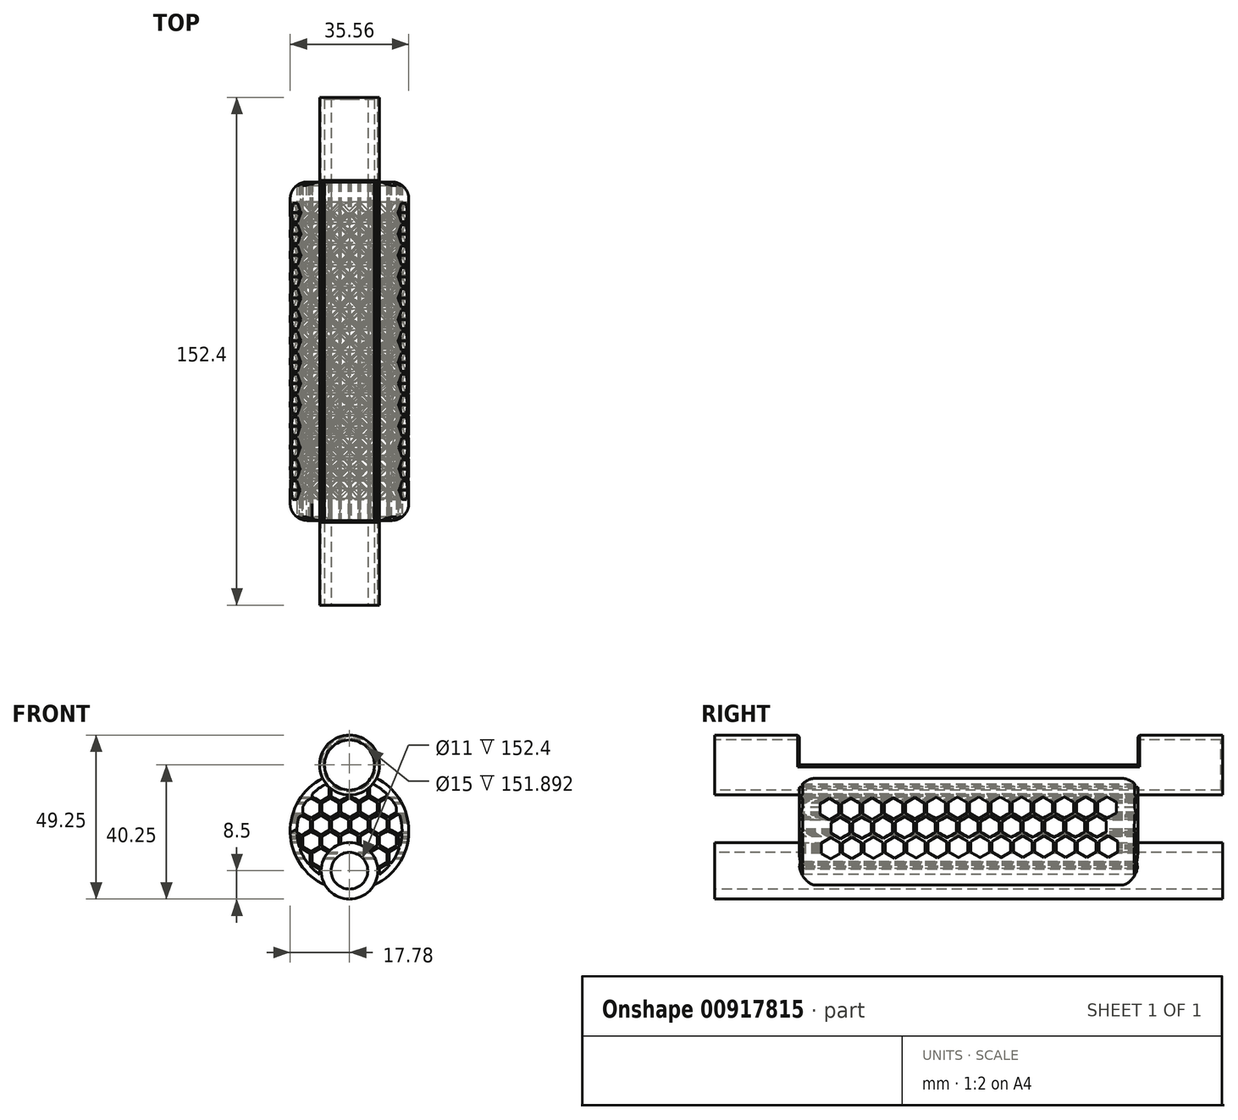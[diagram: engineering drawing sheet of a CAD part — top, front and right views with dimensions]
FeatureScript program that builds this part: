
annotation { "Feature Type Name" : "Feature", "Feature Type Description" : "" }
export const myFeature = defineFeature(function(context is Context, id is Id, definition is map)
    precondition{}
    {
        {
            var Q0;
            Q0=qCreatedBy(makeId("Front.planeOp"),FACE);
            var sketch = newSketch(context, id + "F0", { "sketchPlane" : qUnion([Q0])});
            skCircle(sketch, "E0", {"center": v(0, 0) * mm, "radius": 9 * mm});
            skCircle(sketch, "E1", {"center": v(0, -31.75) * mm, "radius": 8.5 * mm});
            skSolve(sketch);
        }
        {
            var Q0;
            Q0=qSketchRegion(id+"FUGsYxlSOq7sT89_0",true);
            var Q1;
            Q1=makeQuery(id+"F0.imprint","IMPRINT",FACE,{"disambiguationData":[TD([[makeQuery(id+"F0.imprint","IMPRINT",EDGE,{"derivedFrom":sQuery(id+"F0.wireOp",EDGE,"E0")}),1.0]])]});
            var Q2;
            Q2=makeQuery(id+"F0.imprint","IMPRINT",FACE,{"disambiguationData":[TD([[makeQuery(id+"F0.imprint","IMPRINT",EDGE,{"derivedFrom":sQuery(id+"F0.wireOp",EDGE,"E1")}),1.0]])]});
            extrude(context, id + "F1", {"entities" : qUnion([Q0, Q1, Q2]), "endBound" : BoundingType.SYMMETRIC, "depth" : 152.4 * mm, "offsetDistance" : 25.4 * mm});
        }
        {
            var Q0;
            Q0=makeQuery(id+"F1.opExtrude","CAP_FACE",FACE,{"disambiguationData":[OSD([sQuery(id+"F0.wireOp",EDGE,"E0")])],"isStart":false});
            var sketch = newSketch(context, id + "F2", { "sketchPlane" : qUnion([Q0])});
            skCircle(sketch, "E2", {"center": v(0, 0) * mm, "radius": 7.5 * mm});
            skSolve(sketch);
        }
        {
            var Q0;
            Q0=qSketchRegion(id+"F2",true);
            extrude(context, id + "F3", {"entities" : qUnion([Q0]), "operationType" : NewBodyOperationType.REMOVE, "endBound" : BoundingType.THROUGH_ALL, "oppositeDirection" : true, "depth" : 25.4 * mm, "offsetDistance" : 25.4 * mm});
        }
        {
            var Q0;
            Q0=makeQuery(id+"F0.imprint","IMPRINT",FACE,{"disambiguationData":[TD([[makeQuery(id+"F0.imprint","IMPRINT",EDGE,{"derivedFrom":sQuery(id+"F0.wireOp",EDGE,"E0")}),1.0]])]});
            var sketch = newSketch(context, id + "F4", { "sketchPlane" : qUnion([Q0])});
            skLineSegment(sketch, "E3.bottom", {"start": v(-11.18, 12.2) * mm, "end": v(12.33, 12.2) * mm});
            skLineSegment(sketch, "E3.top", {"start": v(-11.18, 0) * mm, "end": v(12.33, 0) * mm});
            skLineSegment(sketch, "E3.left", {"start": v(-11.18, 12.2) * mm, "end": v(-11.18, 0) * mm});
            skLineSegment(sketch, "E3.right", {"start": v(12.33, 12.2) * mm, "end": v(12.33, 0) * mm});
            skSolve(sketch);
        }
        {
            var Q0;
            Q0=qSketchRegion(id+"F4",true);
            extrude(context, id + "F5", {"entities" : qUnion([Q0]), "operationType" : NewBodyOperationType.REMOVE, "endBound" : BoundingType.SYMMETRIC, "oppositeDirection" : true, "depth" : 101.6 * mm, "offsetDistance" : 25.4 * mm});
        }
        {
            var Q0;
            Q0=makeQuery(id+"F5.boolean.opBoolean","INTERSECT",EDGE,{"disambiguationData":[OD(0.0)],"derivedFrom":[makeQuery(id+"F1.opExtrude","SWEPT_FACE",FACE,{"disambiguationData":[OSD([sQuery(id+"F0.wireOp",EDGE,"E0")])]}),makeQuery(id+"F5.opExtrude","SWEPT_FACE",FACE,{"disambiguationData":[OSD([sQuery(id+"F4.wireOp",EDGE,"E3.top")])]})]});
            var Q1;
            Q1=makeQuery(id+"F5.boolean.opBoolean","INTERSECT",EDGE,{"disambiguationData":[OD(1.0)],"derivedFrom":[makeQuery(id+"F1.opExtrude","SWEPT_FACE",FACE,{"disambiguationData":[OSD([sQuery(id+"F0.wireOp",EDGE,"E0")])]}),makeQuery(id+"F5.opExtrude","SWEPT_FACE",FACE,{"disambiguationData":[OSD([sQuery(id+"F4.wireOp",EDGE,"E3.top")])]})]});
            var Q2;
            Q2=makeQuery(id+"F5.boolean.opBoolean","INTERSECT",EDGE,{"disambiguationData":[OD(1.0)],"derivedFrom":[makeQuery(id+"F3.boolean.opBoolean","COPY",FACE,{"derivedFrom":makeQuery(id+"F3.opExtrude","SWEPT_FACE",FACE,{"disambiguationData":[OSD([sQuery(id+"F2.wireOp",EDGE,"E2")])]})}),makeQuery(id+"F5.opExtrude","SWEPT_FACE",FACE,{"disambiguationData":[OSD([sQuery(id+"F4.wireOp",EDGE,"E3.top")])]})]});
            var Q3;
            Q3=makeQuery(id+"F5.boolean.opBoolean","INTERSECT",EDGE,{"disambiguationData":[OD(0.0)],"derivedFrom":[makeQuery(id+"F3.boolean.opBoolean","COPY",FACE,{"derivedFrom":makeQuery(id+"F3.opExtrude","SWEPT_FACE",FACE,{"disambiguationData":[OSD([sQuery(id+"F2.wireOp",EDGE,"E2")])]})}),makeQuery(id+"F5.opExtrude","SWEPT_FACE",FACE,{"disambiguationData":[OSD([sQuery(id+"F4.wireOp",EDGE,"E3.top")])]})]});
            var Q4;
            Q4=makeQuery(id+"F5.boolean.opBoolean","INTERSECT",EDGE,{"derivedFrom":[makeQuery(id+"F1.opExtrude","SWEPT_FACE",FACE,{"disambiguationData":[OSD([sQuery(id+"F0.wireOp",EDGE,"E0")])]}),makeQuery(id+"F5.opExtrude","CAP_FACE",FACE,{"disambiguationData":[OSD([sQuery(id+"F4.wireOp",EDGE,"E3.bottom"),sQuery(id+"F4.wireOp",EDGE,"E3.top"),sQuery(id+"F4.wireOp",EDGE,"E3.left"),sQuery(id+"F4.wireOp",EDGE,"E3.right")])],"isStart":true})]});
            var Q5;
            Q5=makeQuery(id+"F5.boolean.opBoolean","INTERSECT",EDGE,{"derivedFrom":[makeQuery(id+"F1.opExtrude","SWEPT_FACE",FACE,{"disambiguationData":[OSD([sQuery(id+"F0.wireOp",EDGE,"E0")])]}),makeQuery(id+"F5.opExtrude","CAP_FACE",FACE,{"disambiguationData":[OSD([sQuery(id+"F4.wireOp",EDGE,"E3.bottom"),sQuery(id+"F4.wireOp",EDGE,"E3.top"),sQuery(id+"F4.wireOp",EDGE,"E3.left"),sQuery(id+"F4.wireOp",EDGE,"E3.right")])],"isStart":false})]});
            var Q6;
            Q6=makeQuery(id+"F5.boolean.opBoolean","INTERSECT",EDGE,{"derivedFrom":[makeQuery(id+"F3.boolean.opBoolean","COPY",FACE,{"derivedFrom":makeQuery(id+"F3.opExtrude","SWEPT_FACE",FACE,{"disambiguationData":[OSD([sQuery(id+"F2.wireOp",EDGE,"E2")])]})}),makeQuery(id+"F5.opExtrude","CAP_FACE",FACE,{"disambiguationData":[OSD([sQuery(id+"F4.wireOp",EDGE,"E3.bottom"),sQuery(id+"F4.wireOp",EDGE,"E3.top"),sQuery(id+"F4.wireOp",EDGE,"E3.left"),sQuery(id+"F4.wireOp",EDGE,"E3.right")])],"isStart":false})]});
            var Q7;
            Q7=makeQuery(id+"F5.boolean.opBoolean","INTERSECT",EDGE,{"derivedFrom":[makeQuery(id+"F3.boolean.opBoolean","COPY",FACE,{"derivedFrom":makeQuery(id+"F3.opExtrude","SWEPT_FACE",FACE,{"disambiguationData":[OSD([sQuery(id+"F2.wireOp",EDGE,"E2")])]})}),makeQuery(id+"F5.opExtrude","CAP_FACE",FACE,{"disambiguationData":[OSD([sQuery(id+"F4.wireOp",EDGE,"E3.bottom"),sQuery(id+"F4.wireOp",EDGE,"E3.top"),sQuery(id+"F4.wireOp",EDGE,"E3.left"),sQuery(id+"F4.wireOp",EDGE,"E3.right")])],"isStart":true})]});
            var Q8;
            Q8=makeQuery(id+"F3.boolean.opBoolean","INTERSECT",EDGE,{"derivedFrom":[makeQuery(id+"F1.opExtrude","CAP_FACE",FACE,{"disambiguationData":[OSD([sQuery(id+"F0.wireOp",EDGE,"E0")])],"isStart":true}),makeQuery(id+"F3.opExtrude","SWEPT_FACE",FACE,{"disambiguationData":[OSD([sQuery(id+"F2.wireOp",EDGE,"E2")])]})]});
            var Q9;
            Q9=makeQuery(id+"F3.boolean.opBoolean","COPY",EDGE,{"derivedFrom":makeQuery(id+"F3.opExtrude","CAP_EDGE",EDGE,{"disambiguationData":[OSD([sQuery(id+"F2.wireOp",EDGE,"E2")])],"isStart":true})});
            chamfer(context, id + "F6", {"entities" : qUnion([Q0, Q1, Q2, Q3, Q4, Q5, Q6, Q7, Q8, Q9]), "width" : 0.5 * mm, "tangentPropagation" : true});
        }
        {
            var Q0;
            Q0=qCreatedBy(makeId("Front.planeOp"),FACE);
            var sketch = newSketch(context, id + "F7", { "sketchPlane" : qUnion([Q0])});
            skLineSegment(sketch, "E4.0", {"start": v(2, -31.75) * mm, "end": v(2, -8.64) * mm});
            skLineSegment(sketch, "E5.0", {"start": v(-2, -31.75) * mm, "end": v(-2, -8.64) * mm});
            skPoint(sketch, "E6.start.orphan", {"position": v(0, -31.75) * mm});
            skLineSegment(sketch, "E7", {"start": v(-2, -31.75) * mm, "end": v(2, -31.75) * mm});
            skLineSegment(sketch, "E8", {"start": v(2, -8.64) * mm, "end": v(-2, -8.64) * mm});
            skSolve(sketch);
        }
        {
            var Q0;
            Q0=qSketchRegion(id+"F7",true);
            extrude(context, id + "F8", {"entities" : qUnion([Q0]), "operationType" : NewBodyOperationType.ADD, "endBound" : BoundingType.SYMMETRIC, "oppositeDirection" : true, "depth" : 101.6 * mm, "offsetDistance" : 25.4 * mm});
        }
        {
            var Q0;
            Q0=qCreatedBy(makeId("Front.planeOp"),FACE);
            var sketch = newSketch(context, id + "F9", { "sketchPlane" : qUnion([Q0])});
            skCircle(sketch, "E9", {"center": v(0, -19.81) * mm, "radius": 17.78 * mm});
            skSolve(sketch);
        }
        {
            var Q0;
            Q0=qSketchRegion(id+"F9",true);
            extrude(context, id + "F10", {"entities" : qUnion([Q0]), "operationType" : NewBodyOperationType.ADD, "endBound" : BoundingType.SYMMETRIC, "depth" : 101.6 * mm, "offsetDistance" : 25.4 * mm});
        }
        {
            var Q0;
            Q0=makeQuery(id+"F0.imprint","IMPRINT",FACE,{"disambiguationData":[TD([[makeQuery(id+"F0.imprint","IMPRINT",EDGE,{"derivedFrom":sQuery(id+"F0.wireOp",EDGE,"E0")}),1.0]])]});
            var sketch = newSketch(context, id + "F11", { "sketchPlane" : qUnion([Q0])});
            skCircle(sketch, "E10", {"center": v(0, 0) * mm, "radius": 7.5 * mm});
            skSolve(sketch);
        }
        {
            var Q0;
            Q0=qSketchRegion(id+"F11",true);
            extrude(context, id + "F12", {"entities" : qUnion([Q0]), "operationType" : NewBodyOperationType.REMOVE, "endBound" : BoundingType.SYMMETRIC, "oppositeDirection" : true, "depth" : 152.4 * mm, "offsetDistance" : 25.4 * mm});
        }
        {
            var Q0;
            Q0=makeQuery(id+"F10.boolean.opBoolean","MERGE",FACE,{"derivedFrom":[makeQuery(id+"F8.opExtrude","CAP_FACE",FACE,{"disambiguationData":[OSD([sQuery(id+"F7.wireOp",EDGE,"E4.0"),sQuery(id+"F7.wireOp",EDGE,"E5.0"),sQuery(id+"F7.wireOp",EDGE,"E7"),sQuery(id+"F7.wireOp",EDGE,"E8")])],"isStart":true}),makeQuery(id+"F10.opExtrude","CAP_FACE",FACE,{"disambiguationData":[OSD([sQuery(id+"F9.wireOp",EDGE,"E9")])],"isStart":false})]});
            var sketch = newSketch(context, id + "F13", { "sketchPlane" : qUnion([Q0])});
            skCircle(sketch, "E11.cCircle", {"center": v(-11.52, -12.94) * mm, "radius": 2.55 * mm, "construction": true});
            skLineSegment(sketch, "E11.0", {"start": v(-8.97, -11.46) * mm, "end": v(-8.97, -14.4) * mm});
            skLineSegment(sketch, "E11.1", {"start": v(-8.97, -14.4) * mm, "end": v(-11.52, -15.88) * mm});
            skLineSegment(sketch, "E11.2", {"start": v(-11.52, -15.88) * mm, "end": v(-14.07, -14.4) * mm});
            skLineSegment(sketch, "E11.3", {"start": v(-14.07, -14.4) * mm, "end": v(-14.07, -11.46) * mm});
            skLineSegment(sketch, "E11.4", {"start": v(-14.07, -11.46) * mm, "end": v(-11.52, -10) * mm});
            skLineSegment(sketch, "E11.5", {"start": v(-11.52, -10) * mm, "end": v(-8.97, -11.46) * mm});
            skPoint(sketch, "E11.0.midPoint", {"position": v(-8.97, -12.94) * mm});
            skLineSegment(sketch, "E12.1.0.0", {"start": v(-5.75, -9.92) * mm, "end": v(-3.2, -11.4) * mm});
            skLineSegment(sketch, "E12.1.0.1", {"start": v(-8.3, -11.4) * mm, "end": v(-5.75, -9.92) * mm});
            skLineSegment(sketch, "E12.1.0.2", {"start": v(-8.3, -14.34) * mm, "end": v(-8.3, -11.4) * mm});
            skLineSegment(sketch, "E12.1.0.3", {"start": v(-5.75, -15.81) * mm, "end": v(-8.3, -14.34) * mm});
            skLineSegment(sketch, "E12.1.0.4", {"start": v(-3.2, -11.4) * mm, "end": v(-3.2, -14.34) * mm});
            skLineSegment(sketch, "E12.1.0.5", {"start": v(-3.2, -14.34) * mm, "end": v(-5.75, -15.81) * mm});
            skLineSegment(sketch, "E12.2.0.0", {"start": v(0.02, -9.85) * mm, "end": v(2.57, -11.33) * mm});
            skLineSegment(sketch, "E12.2.0.1", {"start": v(-2.53, -11.33) * mm, "end": v(0.02, -9.85) * mm});
            skLineSegment(sketch, "E12.2.0.2", {"start": v(-2.53, -14.27) * mm, "end": v(-2.53, -11.33) * mm});
            skLineSegment(sketch, "E12.2.0.3", {"start": v(0.02, -15.74) * mm, "end": v(-2.53, -14.27) * mm});
            skLineSegment(sketch, "E12.2.0.4", {"start": v(2.57, -11.33) * mm, "end": v(2.57, -14.27) * mm});
            skLineSegment(sketch, "E12.2.0.5", {"start": v(2.57, -14.27) * mm, "end": v(0.02, -15.74) * mm});
            skLineSegment(sketch, "E12.3.0.0", {"start": v(5.78, -9.79) * mm, "end": v(8.33, -11.26) * mm});
            skLineSegment(sketch, "E12.3.0.1", {"start": v(3.23, -11.26) * mm, "end": v(5.78, -9.79) * mm});
            skLineSegment(sketch, "E12.3.0.2", {"start": v(3.23, -14.2) * mm, "end": v(3.23, -11.26) * mm});
            skLineSegment(sketch, "E12.3.0.3", {"start": v(5.78, -15.67) * mm, "end": v(3.23, -14.2) * mm});
            skLineSegment(sketch, "E12.3.0.4", {"start": v(8.33, -11.26) * mm, "end": v(8.33, -14.2) * mm});
            skLineSegment(sketch, "E12.3.0.5", {"start": v(8.33, -14.2) * mm, "end": v(5.78, -15.67) * mm});
            skLineSegment(sketch, "E12.4.0.0", {"start": v(11.55, -9.72) * mm, "end": v(14.1, -11.19) * mm});
            skLineSegment(sketch, "E12.4.0.1", {"start": v(9, -11.19) * mm, "end": v(11.55, -9.72) * mm});
            skLineSegment(sketch, "E12.4.0.2", {"start": v(9, -14.13) * mm, "end": v(9, -11.19) * mm});
            skLineSegment(sketch, "E12.4.0.3", {"start": v(11.55, -15.6) * mm, "end": v(9, -14.13) * mm});
            skLineSegment(sketch, "E12.4.0.4", {"start": v(14.1, -11.19) * mm, "end": v(14.1, -14.13) * mm});
            skLineSegment(sketch, "E12.4.0.5", {"start": v(14.1, -14.13) * mm, "end": v(11.55, -15.6) * mm});
            skLineSegment(sketch, "E12.direction1", {"start": v(-11.52, -10) * mm, "end": v(-5.75, -9.92) * mm, "construction": true});
            skSolve(sketch);
        }
        {
            var Q0;
            Q0=qSketchRegion(id+"F13",true);
            extrude(context, id + "F14", {"entities" : qUnion([Q0]), "operationType" : NewBodyOperationType.REMOVE, "oppositeDirection" : true, "depth" : 177.8 * mm, "offsetDistance" : 25.4 * mm});
        }
        {
            var Q0;
            Q0=makeQuery(id+"F10.boolean.opBoolean","MERGE",FACE,{"derivedFrom":[makeQuery(id+"F8.opExtrude","CAP_FACE",FACE,{"disambiguationData":[OSD([sQuery(id+"F7.wireOp",EDGE,"E4.0"),sQuery(id+"F7.wireOp",EDGE,"E5.0"),sQuery(id+"F7.wireOp",EDGE,"E7"),sQuery(id+"F7.wireOp",EDGE,"E8")])],"isStart":true}),makeQuery(id+"F10.opExtrude","CAP_FACE",FACE,{"disambiguationData":[OSD([sQuery(id+"F9.wireOp",EDGE,"E9")])],"isStart":false})]});
            var sketch = newSketch(context, id + "F15", { "sketchPlane" : qUnion([Q0])});
            skCircle(sketch, "E13.cCircle", {"center": v(-14.33, -18.09) * mm, "radius": 2.55 * mm, "construction": true});
            skLineSegment(sketch, "E13.0", {"start": v(-11.78, -16.61) * mm, "end": v(-11.78, -19.56) * mm});
            skLineSegment(sketch, "E13.1", {"start": v(-11.78, -19.56) * mm, "end": v(-14.33, -21.03) * mm});
            skLineSegment(sketch, "E13.2", {"start": v(-14.33, -21.03) * mm, "end": v(-16.88, -19.56) * mm});
            skLineSegment(sketch, "E13.3", {"start": v(-16.88, -19.56) * mm, "end": v(-16.88, -16.61) * mm});
            skLineSegment(sketch, "E13.4", {"start": v(-16.88, -16.61) * mm, "end": v(-14.33, -15.14) * mm});
            skLineSegment(sketch, "E13.5", {"start": v(-14.33, -15.14) * mm, "end": v(-11.78, -16.61) * mm});
            skPoint(sketch, "E13.0.midPoint", {"position": v(-11.78, -18.09) * mm});
            skLineSegment(sketch, "E14.1.0.0", {"start": v(-8.56, -15.07) * mm, "end": v(-6.01, -16.55) * mm});
            skLineSegment(sketch, "E14.1.0.1", {"start": v(-11.11, -16.55) * mm, "end": v(-8.56, -15.07) * mm});
            skLineSegment(sketch, "E14.1.0.2", {"start": v(-11.11, -19.5) * mm, "end": v(-11.11, -16.55) * mm});
            skLineSegment(sketch, "E14.1.0.3", {"start": v(-8.56, -20.96) * mm, "end": v(-11.11, -19.5) * mm});
            skLineSegment(sketch, "E14.1.0.4", {"start": v(-6.01, -16.55) * mm, "end": v(-6.01, -19.5) * mm});
            skLineSegment(sketch, "E14.1.0.5", {"start": v(-6.01, -19.5) * mm, "end": v(-8.56, -20.96) * mm});
            skLineSegment(sketch, "E14.2.0.0", {"start": v(-2.8, -15) * mm, "end": v(-0.25, -16.48) * mm});
            skLineSegment(sketch, "E14.2.0.1", {"start": v(-5.35, -16.48) * mm, "end": v(-2.8, -15) * mm});
            skLineSegment(sketch, "E14.2.0.2", {"start": v(-5.35, -19.42) * mm, "end": v(-5.35, -16.48) * mm});
            skLineSegment(sketch, "E14.2.0.3", {"start": v(-2.8, -20.9) * mm, "end": v(-5.35, -19.42) * mm});
            skLineSegment(sketch, "E14.2.0.4", {"start": v(-0.25, -16.48) * mm, "end": v(-0.25, -19.42) * mm});
            skLineSegment(sketch, "E14.2.0.5", {"start": v(-0.25, -19.42) * mm, "end": v(-2.8, -20.9) * mm});
            skLineSegment(sketch, "E14.3.0.0", {"start": v(2.97, -14.94) * mm, "end": v(5.52, -16.4) * mm});
            skLineSegment(sketch, "E14.3.0.1", {"start": v(0.42, -16.4) * mm, "end": v(2.97, -14.94) * mm});
            skLineSegment(sketch, "E14.3.0.2", {"start": v(0.42, -19.35) * mm, "end": v(0.42, -16.4) * mm});
            skLineSegment(sketch, "E14.3.0.3", {"start": v(2.97, -20.83) * mm, "end": v(0.42, -19.35) * mm});
            skLineSegment(sketch, "E14.3.0.4", {"start": v(5.52, -16.4) * mm, "end": v(5.52, -19.35) * mm});
            skLineSegment(sketch, "E14.3.0.5", {"start": v(5.52, -19.35) * mm, "end": v(2.97, -20.83) * mm});
            skLineSegment(sketch, "E14.4.0.0", {"start": v(8.73, -14.87) * mm, "end": v(11.28, -16.34) * mm});
            skLineSegment(sketch, "E14.4.0.1", {"start": v(6.18, -16.34) * mm, "end": v(8.73, -14.87) * mm});
            skLineSegment(sketch, "E14.4.0.2", {"start": v(6.18, -19.28) * mm, "end": v(6.18, -16.34) * mm});
            skLineSegment(sketch, "E14.4.0.3", {"start": v(8.73, -20.76) * mm, "end": v(6.18, -19.28) * mm});
            skLineSegment(sketch, "E14.4.0.4", {"start": v(11.28, -16.34) * mm, "end": v(11.28, -19.28) * mm});
            skLineSegment(sketch, "E14.4.0.5", {"start": v(11.28, -19.28) * mm, "end": v(8.73, -20.76) * mm});
            skLineSegment(sketch, "E14.direction1", {"start": v(-14.33, -15.14) * mm, "end": v(-8.56, -15.07) * mm, "construction": true});
            skLineSegment(sketch, "E15.0.5.0", {"start": v(14.5, -14.8) * mm, "end": v(17.05, -16.27) * mm});
            skLineSegment(sketch, "E15.3.5.0", {"start": v(11.95, -16.27) * mm, "end": v(14.5, -14.8) * mm});
            skLineSegment(sketch, "E15.6.5.0", {"start": v(11.95, -19.22) * mm, "end": v(11.95, -16.27) * mm});
            skLineSegment(sketch, "E15.9.5.0", {"start": v(14.5, -20.69) * mm, "end": v(11.95, -19.22) * mm});
            skLineSegment(sketch, "E15.12.5.0", {"start": v(17.05, -16.27) * mm, "end": v(17.05, -19.22) * mm});
            skLineSegment(sketch, "E15.15.5.0", {"start": v(17.05, -19.22) * mm, "end": v(14.5, -20.69) * mm});
            skSolve(sketch);
        }
        {
            var Q0;
            Q0=qSketchRegion(id+"F15",true);
            extrude(context, id + "F16", {"entities" : qUnion([Q0]), "operationType" : NewBodyOperationType.REMOVE, "oppositeDirection" : true, "depth" : 177.8 * mm, "offsetDistance" : 25.4 * mm});
        }
        {
            var Q0;
            Q0=makeQuery(id+"F10.boolean.opBoolean","MERGE",FACE,{"derivedFrom":[makeQuery(id+"F8.opExtrude","CAP_FACE",FACE,{"disambiguationData":[OSD([sQuery(id+"F7.wireOp",EDGE,"E4.0"),sQuery(id+"F7.wireOp",EDGE,"E5.0"),sQuery(id+"F7.wireOp",EDGE,"E7"),sQuery(id+"F7.wireOp",EDGE,"E8")])],"isStart":true}),makeQuery(id+"F10.opExtrude","CAP_FACE",FACE,{"disambiguationData":[OSD([sQuery(id+"F9.wireOp",EDGE,"E9")])],"isStart":false})]});
            var sketch = newSketch(context, id + "F17", { "sketchPlane" : qUnion([Q0])});
            skCircle(sketch, "E16.cCircle", {"center": v(-17.3, -23) * mm, "radius": 2.55 * mm, "construction": true});
            skLineSegment(sketch, "E16.0", {"start": v(-14.75, -21.52) * mm, "end": v(-14.75, -24.47) * mm});
            skLineSegment(sketch, "E16.1", {"start": v(-14.75, -24.47) * mm, "end": v(-17.3, -25.94) * mm});
            skLineSegment(sketch, "E16.2", {"start": v(-17.3, -25.94) * mm, "end": v(-19.84, -24.47) * mm});
            skLineSegment(sketch, "E16.3", {"start": v(-19.84, -24.47) * mm, "end": v(-19.84, -21.52) * mm});
            skLineSegment(sketch, "E16.4", {"start": v(-19.84, -21.52) * mm, "end": v(-17.3, -20.05) * mm});
            skLineSegment(sketch, "E16.5", {"start": v(-17.3, -20.05) * mm, "end": v(-14.75, -21.52) * mm});
            skPoint(sketch, "E16.0.midPoint", {"position": v(-14.75, -23) * mm});
            skLineSegment(sketch, "E17.1.0.0", {"start": v(-11.53, -19.98) * mm, "end": v(-8.98, -21.46) * mm});
            skLineSegment(sketch, "E17.1.0.1", {"start": v(-14.08, -21.46) * mm, "end": v(-11.53, -19.98) * mm});
            skLineSegment(sketch, "E17.1.0.2", {"start": v(-14.08, -24.4) * mm, "end": v(-14.08, -21.46) * mm});
            skLineSegment(sketch, "E17.1.0.3", {"start": v(-11.53, -25.87) * mm, "end": v(-14.08, -24.4) * mm});
            skLineSegment(sketch, "E17.1.0.4", {"start": v(-8.98, -21.46) * mm, "end": v(-8.98, -24.4) * mm});
            skLineSegment(sketch, "E17.1.0.5", {"start": v(-8.98, -24.4) * mm, "end": v(-11.53, -25.87) * mm});
            skLineSegment(sketch, "E17.direction1", {"start": v(-17.3, -20.05) * mm, "end": v(-11.53, -19.98) * mm, "construction": true});
            skLineSegment(sketch, "E18.0.2.0", {"start": v(-5.76, -19.91) * mm, "end": v(-3.21, -21.39) * mm});
            skLineSegment(sketch, "E18.3.2.0", {"start": v(-8.31, -21.39) * mm, "end": v(-5.76, -19.91) * mm});
            skLineSegment(sketch, "E18.6.2.0", {"start": v(-8.31, -24.33) * mm, "end": v(-8.31, -21.39) * mm});
            skLineSegment(sketch, "E18.9.2.0", {"start": v(-5.76, -25.8) * mm, "end": v(-8.31, -24.33) * mm});
            skLineSegment(sketch, "E18.12.2.0", {"start": v(-3.21, -21.39) * mm, "end": v(-3.21, -24.33) * mm});
            skLineSegment(sketch, "E18.15.2.0", {"start": v(-3.21, -24.33) * mm, "end": v(-5.76, -25.8) * mm});
            skLineSegment(sketch, "E18.0.3.0", {"start": v(0, -19.85) * mm, "end": v(2.55, -21.32) * mm});
            skLineSegment(sketch, "E18.3.3.0", {"start": v(-2.55, -21.32) * mm, "end": v(0, -19.85) * mm});
            skLineSegment(sketch, "E18.6.3.0", {"start": v(-2.55, -24.26) * mm, "end": v(-2.55, -21.32) * mm});
            skLineSegment(sketch, "E18.9.3.0", {"start": v(0, -25.74) * mm, "end": v(-2.55, -24.26) * mm});
            skLineSegment(sketch, "E18.12.3.0", {"start": v(2.55, -21.32) * mm, "end": v(2.55, -24.26) * mm});
            skLineSegment(sketch, "E18.15.3.0", {"start": v(2.55, -24.26) * mm, "end": v(0, -25.74) * mm});
            skLineSegment(sketch, "E18.0.4.0", {"start": v(5.77, -19.78) * mm, "end": v(8.32, -21.25) * mm});
            skLineSegment(sketch, "E18.3.4.0", {"start": v(3.22, -21.25) * mm, "end": v(5.77, -19.78) * mm});
            skLineSegment(sketch, "E18.6.4.0", {"start": v(3.22, -24.2) * mm, "end": v(3.22, -21.25) * mm});
            skLineSegment(sketch, "E18.9.4.0", {"start": v(5.77, -25.67) * mm, "end": v(3.22, -24.2) * mm});
            skLineSegment(sketch, "E18.12.4.0", {"start": v(8.32, -21.25) * mm, "end": v(8.32, -24.2) * mm});
            skLineSegment(sketch, "E18.15.4.0", {"start": v(8.32, -24.2) * mm, "end": v(5.77, -25.67) * mm});
            skLineSegment(sketch, "E19.0.5.0", {"start": v(11.53, -19.7) * mm, "end": v(14.08, -21.18) * mm});
            skLineSegment(sketch, "E19.3.5.0", {"start": v(8.98, -21.18) * mm, "end": v(11.53, -19.7) * mm});
            skLineSegment(sketch, "E19.6.5.0", {"start": v(8.98, -24.13) * mm, "end": v(8.98, -21.18) * mm});
            skLineSegment(sketch, "E19.9.5.0", {"start": v(11.53, -25.6) * mm, "end": v(8.98, -24.13) * mm});
            skLineSegment(sketch, "E19.12.5.0", {"start": v(14.08, -21.18) * mm, "end": v(14.08, -24.13) * mm});
            skLineSegment(sketch, "E19.15.5.0", {"start": v(14.08, -24.13) * mm, "end": v(11.53, -25.6) * mm});
            skLineSegment(sketch, "E20.0.6.0", {"start": v(17.3, -19.64) * mm, "end": v(19.85, -21.11) * mm});
            skLineSegment(sketch, "E20.3.6.0", {"start": v(14.75, -21.11) * mm, "end": v(17.3, -19.64) * mm});
            skLineSegment(sketch, "E20.6.6.0", {"start": v(14.75, -24.06) * mm, "end": v(14.75, -21.11) * mm});
            skLineSegment(sketch, "E20.9.6.0", {"start": v(17.3, -25.53) * mm, "end": v(14.75, -24.06) * mm});
            skLineSegment(sketch, "E20.12.6.0", {"start": v(19.85, -21.11) * mm, "end": v(19.85, -24.06) * mm});
            skLineSegment(sketch, "E20.15.6.0", {"start": v(19.85, -24.06) * mm, "end": v(17.3, -25.53) * mm});
            skSolve(sketch);
        }
        {
            var Q0;
            {var subQ6=sQuery(id+"F17.wireOp",EDGE,"E16.0");Q0=makeQuery(id+"F17.imprint","IMPRINT",FACE,{"disambiguationData":[TD([[makeQuery(id+"F17.imprint","IMPRINT",EDGE,{"derivedFrom":subQ6}),-1.0]])]});}
            var Q1;
            Q1=makeQuery(id+"F17.imprint","IMPRINT",FACE,{"disambiguationData":[TD([[makeQuery(id+"F17.imprint","IMPRINT",EDGE,{"derivedFrom":sQuery(id+"F17.wireOp",EDGE,"E17.1.0.0")}),-1.0]])]});
            var Q2;
            {var subQ4=sQuery(id+"F17.wireOp",EDGE,"E18.0.2.0");Q2=makeQuery(id+"F17.imprint","IMPRINT",FACE,{"disambiguationData":[TD([[makeQuery(id+"F17.imprint","IMPRINT",EDGE,{"derivedFrom":subQ4}),-1.0]])]});}
            var Q3;
            {var subQ5=sQuery(id+"F17.wireOp",EDGE,"E18.0.3.0");Q3=makeQuery(id+"F17.imprint","IMPRINT",FACE,{"disambiguationData":[TD([[makeQuery(id+"F17.imprint","IMPRINT",EDGE,{"derivedFrom":subQ5}),-1.0]])]});}
            var Q4;
            Q4=makeQuery(id+"F17.imprint","IMPRINT",FACE,{"disambiguationData":[TD([[makeQuery(id+"F17.imprint","IMPRINT",EDGE,{"derivedFrom":sQuery(id+"F17.wireOp",EDGE,"E18.0.4.0")}),-1.0]])]});
            var Q5;
            Q5=makeQuery(id+"F17.imprint","IMPRINT",FACE,{"disambiguationData":[TD([[makeQuery(id+"F17.imprint","IMPRINT",EDGE,{"derivedFrom":sQuery(id+"F17.wireOp",EDGE,"E19.0.5.0")}),-1.0]])]});
            var Q6;
            {var subQ1=sQuery(id+"F17.wireOp",EDGE,"E20.3.6.0");Q6=makeQuery(id+"F17.imprint","IMPRINT",FACE,{"disambiguationData":[TD([[makeQuery(id+"F17.imprint","IMPRINT",EDGE,{"derivedFrom":subQ1}),-1.0]])]});}
            extrude(context, id + "F18", {"entities" : qUnion([Q0, Q1, Q2, Q3, Q4, Q5, Q6]), "operationType" : NewBodyOperationType.REMOVE, "oppositeDirection" : true, "depth" : 101.6 * mm, "offsetDistance" : 25.4 * mm});
        }
        {
            var Q0;
            Q0=makeQuery(id+"F10.boolean.opBoolean","MERGE",FACE,{"derivedFrom":[makeQuery(id+"F8.opExtrude","CAP_FACE",FACE,{"disambiguationData":[OSD([sQuery(id+"F7.wireOp",EDGE,"E4.0"),sQuery(id+"F7.wireOp",EDGE,"E5.0"),sQuery(id+"F7.wireOp",EDGE,"E7"),sQuery(id+"F7.wireOp",EDGE,"E8")])],"isStart":true}),makeQuery(id+"F10.opExtrude","CAP_FACE",FACE,{"disambiguationData":[OSD([sQuery(id+"F9.wireOp",EDGE,"E9")])],"isStart":false})]});
            var sketch = newSketch(context, id + "F19", { "sketchPlane" : qUnion([Q0])});
            skCircle(sketch, "E21.cCircle", {"center": v(-14.4, -27.92) * mm, "radius": 2.55 * mm, "construction": true});
            skLineSegment(sketch, "E21.0", {"start": v(-11.84, -26.45) * mm, "end": v(-11.84, -29.4) * mm});
            skLineSegment(sketch, "E21.1", {"start": v(-11.84, -29.4) * mm, "end": v(-14.4, -30.86) * mm});
            skLineSegment(sketch, "E21.2", {"start": v(-14.4, -30.86) * mm, "end": v(-16.94, -29.4) * mm});
            skLineSegment(sketch, "E21.3", {"start": v(-16.94, -29.4) * mm, "end": v(-16.94, -26.45) * mm});
            skLineSegment(sketch, "E21.4", {"start": v(-16.94, -26.45) * mm, "end": v(-14.4, -24.98) * mm});
            skLineSegment(sketch, "E21.5", {"start": v(-14.4, -24.98) * mm, "end": v(-11.84, -26.45) * mm});
            skPoint(sketch, "E21.0.midPoint", {"position": v(-11.84, -27.92) * mm});
            skLineSegment(sketch, "E22.1.0.0", {"start": v(-8.63, -24.9) * mm, "end": v(-6.08, -26.38) * mm});
            skLineSegment(sketch, "E22.1.0.1", {"start": v(-11.18, -26.38) * mm, "end": v(-8.63, -24.9) * mm});
            skLineSegment(sketch, "E22.1.0.2", {"start": v(-11.18, -29.32) * mm, "end": v(-11.18, -26.38) * mm});
            skLineSegment(sketch, "E22.1.0.3", {"start": v(-8.63, -30.8) * mm, "end": v(-11.18, -29.32) * mm});
            skLineSegment(sketch, "E22.1.0.4", {"start": v(-6.08, -26.38) * mm, "end": v(-6.08, -29.32) * mm});
            skLineSegment(sketch, "E22.1.0.5", {"start": v(-6.08, -29.32) * mm, "end": v(-8.63, -30.8) * mm});
            skLineSegment(sketch, "E22.2.0.0", {"start": v(-2.86, -24.84) * mm, "end": v(-0.31, -26.31) * mm});
            skLineSegment(sketch, "E22.2.0.1", {"start": v(-5.41, -26.31) * mm, "end": v(-2.86, -24.84) * mm});
            skLineSegment(sketch, "E22.2.0.2", {"start": v(-5.41, -29.25) * mm, "end": v(-5.41, -26.31) * mm});
            skLineSegment(sketch, "E22.2.0.3", {"start": v(-2.86, -30.73) * mm, "end": v(-5.41, -29.25) * mm});
            skLineSegment(sketch, "E22.2.0.4", {"start": v(-0.31, -26.31) * mm, "end": v(-0.31, -29.25) * mm});
            skLineSegment(sketch, "E22.2.0.5", {"start": v(-0.31, -29.25) * mm, "end": v(-2.86, -30.73) * mm});
            skLineSegment(sketch, "E22.3.0.0", {"start": v(2.9, -24.77) * mm, "end": v(5.45, -26.24) * mm});
            skLineSegment(sketch, "E22.3.0.1", {"start": v(0.35, -26.24) * mm, "end": v(2.9, -24.77) * mm});
            skLineSegment(sketch, "E22.3.0.2", {"start": v(0.35, -29.19) * mm, "end": v(0.35, -26.24) * mm});
            skLineSegment(sketch, "E22.3.0.3", {"start": v(2.9, -30.66) * mm, "end": v(0.35, -29.19) * mm});
            skLineSegment(sketch, "E22.3.0.4", {"start": v(5.45, -26.24) * mm, "end": v(5.45, -29.19) * mm});
            skLineSegment(sketch, "E22.3.0.5", {"start": v(5.45, -29.19) * mm, "end": v(2.9, -30.66) * mm});
            skLineSegment(sketch, "E22.4.0.0", {"start": v(8.67, -24.7) * mm, "end": v(11.22, -26.17) * mm});
            skLineSegment(sketch, "E22.4.0.1", {"start": v(6.12, -26.17) * mm, "end": v(8.67, -24.7) * mm});
            skLineSegment(sketch, "E22.4.0.2", {"start": v(6.12, -29.12) * mm, "end": v(6.12, -26.17) * mm});
            skLineSegment(sketch, "E22.4.0.3", {"start": v(8.67, -30.6) * mm, "end": v(6.12, -29.12) * mm});
            skLineSegment(sketch, "E22.4.0.4", {"start": v(11.22, -26.17) * mm, "end": v(11.22, -29.12) * mm});
            skLineSegment(sketch, "E22.4.0.5", {"start": v(11.22, -29.12) * mm, "end": v(8.67, -30.6) * mm});
            skLineSegment(sketch, "E22.direction1", {"start": v(-14.4, -24.98) * mm, "end": v(-8.63, -24.9) * mm, "construction": true});
            skLineSegment(sketch, "E23.0.5.0", {"start": v(14.44, -24.63) * mm, "end": v(16.99, -26.1) * mm});
            skLineSegment(sketch, "E23.3.5.0", {"start": v(11.89, -26.1) * mm, "end": v(14.44, -24.63) * mm});
            skLineSegment(sketch, "E23.6.5.0", {"start": v(11.89, -29.05) * mm, "end": v(11.89, -26.1) * mm});
            skLineSegment(sketch, "E23.9.5.0", {"start": v(14.44, -30.52) * mm, "end": v(11.89, -29.05) * mm});
            skLineSegment(sketch, "E23.12.5.0", {"start": v(16.99, -26.1) * mm, "end": v(16.99, -29.05) * mm});
            skLineSegment(sketch, "E23.15.5.0", {"start": v(16.99, -29.05) * mm, "end": v(14.44, -30.52) * mm});
            skSolve(sketch);
        }
        {
            var Q0;
            Q0=makeQuery(id+"F19.imprint","IMPRINT",FACE,{"disambiguationData":[TD([[makeQuery(id+"F19.imprint","IMPRINT",EDGE,{"derivedFrom":sQuery(id+"F19.wireOp",EDGE,"E21.0")}),1.0]])]});
            var sketch = newSketch(context, id + "F20", { "sketchPlane" : qUnion([Q0])});
            skCircle(sketch, "E24.cCircle", {"center": v(-8.71, -8) * mm, "radius": 2.55 * mm, "construction": true});
            skLineSegment(sketch, "E24.0", {"start": v(-6.16, -6.53) * mm, "end": v(-6.16, -9.47) * mm});
            skLineSegment(sketch, "E24.1", {"start": v(-6.16, -9.47) * mm, "end": v(-8.71, -10.94) * mm});
            skLineSegment(sketch, "E24.2", {"start": v(-8.71, -10.94) * mm, "end": v(-11.26, -9.47) * mm});
            skLineSegment(sketch, "E24.3", {"start": v(-11.26, -9.47) * mm, "end": v(-11.26, -6.53) * mm});
            skLineSegment(sketch, "E24.4", {"start": v(-11.26, -6.53) * mm, "end": v(-8.71, -5.06) * mm});
            skLineSegment(sketch, "E24.5", {"start": v(-8.71, -5.06) * mm, "end": v(-6.16, -6.53) * mm});
            skPoint(sketch, "E24.0.midPoint", {"position": v(-6.16, -8) * mm});
            skLineSegment(sketch, "E25.1.0.0", {"start": v(-2.95, -4.99) * mm, "end": v(-0.4, -6.46) * mm});
            skLineSegment(sketch, "E25.1.0.1", {"start": v(-5.5, -6.46) * mm, "end": v(-2.95, -4.99) * mm});
            skLineSegment(sketch, "E25.1.0.2", {"start": v(-5.5, -9.4) * mm, "end": v(-5.5, -6.46) * mm});
            skLineSegment(sketch, "E25.1.0.3", {"start": v(-2.95, -10.88) * mm, "end": v(-5.5, -9.4) * mm});
            skLineSegment(sketch, "E25.1.0.4", {"start": v(-0.4, -6.46) * mm, "end": v(-0.4, -9.4) * mm});
            skLineSegment(sketch, "E25.1.0.5", {"start": v(-0.4, -9.4) * mm, "end": v(-2.95, -10.88) * mm});
            skLineSegment(sketch, "E25.2.0.0", {"start": v(2.82, -4.92) * mm, "end": v(5.37, -6.4) * mm});
            skLineSegment(sketch, "E25.2.0.1", {"start": v(0.27, -6.4) * mm, "end": v(2.82, -4.92) * mm});
            skLineSegment(sketch, "E25.2.0.2", {"start": v(0.27, -9.34) * mm, "end": v(0.27, -6.4) * mm});
            skLineSegment(sketch, "E25.2.0.3", {"start": v(2.82, -10.8) * mm, "end": v(0.27, -9.34) * mm});
            skLineSegment(sketch, "E25.2.0.4", {"start": v(5.37, -6.4) * mm, "end": v(5.37, -9.34) * mm});
            skLineSegment(sketch, "E25.2.0.5", {"start": v(5.37, -9.34) * mm, "end": v(2.82, -10.8) * mm});
            skLineSegment(sketch, "E25.3.0.0", {"start": v(8.59, -4.85) * mm, "end": v(11.14, -6.32) * mm});
            skLineSegment(sketch, "E25.3.0.1", {"start": v(6.04, -6.32) * mm, "end": v(8.59, -4.85) * mm});
            skLineSegment(sketch, "E25.3.0.2", {"start": v(6.04, -9.27) * mm, "end": v(6.04, -6.32) * mm});
            skLineSegment(sketch, "E25.3.0.3", {"start": v(8.59, -10.74) * mm, "end": v(6.04, -9.27) * mm});
            skLineSegment(sketch, "E25.3.0.4", {"start": v(11.14, -6.32) * mm, "end": v(11.14, -9.27) * mm});
            skLineSegment(sketch, "E25.3.0.5", {"start": v(11.14, -9.27) * mm, "end": v(8.59, -10.74) * mm});
            skLineSegment(sketch, "E25.direction1", {"start": v(-8.71, -5.06) * mm, "end": v(-2.95, -4.99) * mm, "construction": true});
            skSolve(sketch);
        }
        {
            var Q0;
            {var subQ30=sQuery(id+"F20.wireOp",EDGE,"E24.1");Q0=makeQuery(id+"F20.imprint","IMPRINT",FACE,{"disambiguationData":[TD([[makeQuery(id+"F20.imprint","IMPRINT",EDGE,{"derivedFrom":subQ30}),1.0]])]});}
            var sketch = newSketch(context, id + "F21", { "sketchPlane" : qUnion([Q0])});
            skCircle(sketch, "E26.cCircle", {"center": v(-11.51, -32.84) * mm, "radius": 2.55 * mm, "construction": true});
            skLineSegment(sketch, "E26.0", {"start": v(-8.96, -31.36) * mm, "end": v(-8.96, -34.3) * mm});
            skLineSegment(sketch, "E26.1", {"start": v(-8.96, -34.3) * mm, "end": v(-11.51, -35.78) * mm});
            skLineSegment(sketch, "E26.2", {"start": v(-11.51, -35.78) * mm, "end": v(-14.06, -34.3) * mm});
            skLineSegment(sketch, "E26.3", {"start": v(-14.06, -34.3) * mm, "end": v(-14.06, -31.36) * mm});
            skLineSegment(sketch, "E26.4", {"start": v(-14.06, -31.36) * mm, "end": v(-11.51, -29.9) * mm});
            skLineSegment(sketch, "E26.5", {"start": v(-11.51, -29.9) * mm, "end": v(-8.96, -31.36) * mm});
            skPoint(sketch, "E26.0.midPoint", {"position": v(-8.96, -32.84) * mm});
            skLineSegment(sketch, "E27.1.0.0", {"start": v(-5.75, -29.82) * mm, "end": v(-3.2, -31.3) * mm});
            skLineSegment(sketch, "E27.1.0.1", {"start": v(-8.3, -31.3) * mm, "end": v(-5.75, -29.82) * mm});
            skLineSegment(sketch, "E27.1.0.2", {"start": v(-8.3, -34.24) * mm, "end": v(-8.3, -31.3) * mm});
            skLineSegment(sketch, "E27.1.0.3", {"start": v(-5.75, -35.71) * mm, "end": v(-8.3, -34.24) * mm});
            skLineSegment(sketch, "E27.1.0.4", {"start": v(-3.2, -31.3) * mm, "end": v(-3.2, -34.24) * mm});
            skLineSegment(sketch, "E27.1.0.5", {"start": v(-3.2, -34.24) * mm, "end": v(-5.75, -35.71) * mm});
            skLineSegment(sketch, "E27.2.0.0", {"start": v(0.02, -29.75) * mm, "end": v(2.57, -31.23) * mm});
            skLineSegment(sketch, "E27.2.0.1", {"start": v(-2.53, -31.23) * mm, "end": v(0.02, -29.75) * mm});
            skLineSegment(sketch, "E27.2.0.2", {"start": v(-2.53, -34.17) * mm, "end": v(-2.53, -31.23) * mm});
            skLineSegment(sketch, "E27.2.0.3", {"start": v(0.02, -35.64) * mm, "end": v(-2.53, -34.17) * mm});
            skLineSegment(sketch, "E27.2.0.4", {"start": v(2.57, -31.23) * mm, "end": v(2.57, -34.17) * mm});
            skLineSegment(sketch, "E27.2.0.5", {"start": v(2.57, -34.17) * mm, "end": v(0.02, -35.64) * mm});
            skLineSegment(sketch, "E27.3.0.0", {"start": v(5.79, -29.69) * mm, "end": v(8.34, -31.16) * mm});
            skLineSegment(sketch, "E27.3.0.1", {"start": v(3.24, -31.16) * mm, "end": v(5.79, -29.69) * mm});
            skLineSegment(sketch, "E27.3.0.2", {"start": v(3.24, -34.1) * mm, "end": v(3.24, -31.16) * mm});
            skLineSegment(sketch, "E27.3.0.3", {"start": v(5.79, -35.57) * mm, "end": v(3.24, -34.1) * mm});
            skLineSegment(sketch, "E27.3.0.4", {"start": v(8.34, -31.16) * mm, "end": v(8.34, -34.1) * mm});
            skLineSegment(sketch, "E27.3.0.5", {"start": v(8.34, -34.1) * mm, "end": v(5.79, -35.57) * mm});
            skLineSegment(sketch, "E27.direction1", {"start": v(-11.51, -29.9) * mm, "end": v(-5.75, -29.82) * mm, "construction": true});
            skLineSegment(sketch, "E28.0.4.0", {"start": v(11.55, -29.62) * mm, "end": v(14.1, -31.09) * mm});
            skLineSegment(sketch, "E28.3.4.0", {"start": v(9, -31.09) * mm, "end": v(11.55, -29.62) * mm});
            skLineSegment(sketch, "E28.6.4.0", {"start": v(9, -34.03) * mm, "end": v(9, -31.09) * mm});
            skLineSegment(sketch, "E28.9.4.0", {"start": v(11.55, -35.5) * mm, "end": v(9, -34.03) * mm});
            skLineSegment(sketch, "E28.12.4.0", {"start": v(14.1, -31.09) * mm, "end": v(14.1, -34.03) * mm});
            skLineSegment(sketch, "E28.15.4.0", {"start": v(14.1, -34.03) * mm, "end": v(11.55, -35.5) * mm});
            skSolve(sketch);
        }
        {
            var Q0;
            {var subQ4=sQuery(id+"F20.wireOp",EDGE,"E25.1.0.3");Q0=makeQuery(id+"F20.imprint","IMPRINT",FACE,{"disambiguationData":[TD([[makeQuery(id+"F20.imprint","IMPRINT",EDGE,{"derivedFrom":subQ4}),-1.0]])]});}
            var Q1;
            {var subQ4=sQuery(id+"F20.wireOp",EDGE,"E25.2.0.3");Q1=makeQuery(id+"F20.imprint","IMPRINT",FACE,{"disambiguationData":[TD([[makeQuery(id+"F20.imprint","IMPRINT",EDGE,{"derivedFrom":subQ4}),-1.0]])]});}
            var Q2;
            {var subQ5=sQuery(id+"F20.wireOp",EDGE,"E25.3.0.0");Q2=makeQuery(id+"F20.imprint","IMPRINT",FACE,{"disambiguationData":[TD([[makeQuery(id+"F20.imprint","IMPRINT",EDGE,{"derivedFrom":subQ5}),-1.0]])]});}
            var Q3;
            {var subQ0=sQuery(id+"F20.wireOp",EDGE,"E24.1");Q3=makeQuery(id+"F20.imprint","IMPRINT",FACE,{"disambiguationData":[TD([[makeQuery(id+"F20.imprint","IMPRINT",EDGE,{"derivedFrom":subQ0}),-1.0]])]});}
            extrude(context, id + "F22", {"entities" : qUnion([Q0, Q1, Q2, Q3]), "operationType" : NewBodyOperationType.REMOVE, "oppositeDirection" : true, "depth" : 152.4 * mm, "offsetDistance" : 25.4 * mm});
        }
        {
            var Q0;
            Q0=makeQuery(id+"F19.imprint","IMPRINT",FACE,{"disambiguationData":[TD([[makeQuery(id+"F19.imprint","IMPRINT",EDGE,{"derivedFrom":sQuery(id+"F19.wireOp",EDGE,"E21.0")}),-1.0]])]});
            var Q1;
            {var subQ11=sQuery(id+"F19.wireOp",EDGE,"E22.1.0.1");Q1=makeQuery(id+"F19.imprint","IMPRINT",FACE,{"disambiguationData":[TD([[makeQuery(id+"F19.imprint","IMPRINT",EDGE,{"derivedFrom":subQ11}),-1.0]])]});}
            var Q2;
            {var subQ10=sQuery(id+"F19.wireOp",EDGE,"E22.4.0.0");Q2=makeQuery(id+"F19.imprint","IMPRINT",FACE,{"disambiguationData":[TD([[makeQuery(id+"F19.imprint","IMPRINT",EDGE,{"derivedFrom":subQ10}),-1.0]])]});}
            var Q3;
            {var subQ1=sQuery(id+"F19.wireOp",EDGE,"E23.0.5.0");Q3=makeQuery(id+"F19.imprint","IMPRINT",FACE,{"disambiguationData":[TD([[makeQuery(id+"F19.imprint","IMPRINT",EDGE,{"derivedFrom":subQ1}),-1.0]])]});}
            var Q4;
            {var subQ11=sQuery(id+"F21.wireOp",EDGE,"E28.0.4.0");Q4=makeQuery(id+"F21.imprint","IMPRINT",FACE,{"disambiguationData":[TD([[makeQuery(id+"F21.imprint","IMPRINT",EDGE,{"derivedFrom":subQ11}),-1.0]])]});}
            var Q5;
            {var subQ2=sQuery(id+"F21.wireOp",EDGE,"E26.0");Q5=makeQuery(id+"F21.imprint","IMPRINT",FACE,{"disambiguationData":[TD([[makeQuery(id+"F21.imprint","IMPRINT",EDGE,{"derivedFrom":subQ2}),-1.0]])]});}
            extrude(context, id + "F23", {"entities" : qUnion([Q0, Q1, Q2, Q3, Q4, Q5]), "operationType" : NewBodyOperationType.REMOVE, "oppositeDirection" : true, "depth" : 152.4 * mm, "offsetDistance" : 25.4 * mm});
        }
        {
            var Q0;
            Q0=makeQuery(id+"F10.boolean.opBoolean","MERGE",FACE,{"derivedFrom":[makeQuery(id+"F8.opExtrude","CAP_FACE",FACE,{"disambiguationData":[OSD([sQuery(id+"F7.wireOp",EDGE,"E4.0"),sQuery(id+"F7.wireOp",EDGE,"E5.0"),sQuery(id+"F7.wireOp",EDGE,"E7"),sQuery(id+"F7.wireOp",EDGE,"E8")])],"isStart":true}),makeQuery(id+"F10.opExtrude","CAP_FACE",FACE,{"disambiguationData":[OSD([sQuery(id+"F9.wireOp",EDGE,"E9")])],"isStart":false})]});
            var sketch = newSketch(context, id + "F24", { "sketchPlane" : qUnion([Q0])});
            skCircle(sketch, "E29", {"center": v(0, -19.85) * mm, "radius": 17.78 * mm});
            skCircle(sketch, "E30.0", {"center": v(0, -19.85) * mm, "radius": 15.78 * mm});
            skSolve(sketch);
        }
        {
            var Q0;
            Q0=qSketchRegion(id+"F24",true);
            extrude(context, id + "F25", {"entities" : qUnion([Q0]), "operationType" : NewBodyOperationType.ADD, "oppositeDirection" : true, "depth" : 101.6 * mm, "offsetDistance" : 25.4 * mm});
        }
        {
            var Q0;
            Q0=makeQuery(id+"F25.boolean.opBoolean","SPLIT",FACE,{"derivedFrom":makeQuery(id+"F25.opExtrude","CAP_FACE",FACE,{"disambiguationData":[OSD([sQuery(id+"F24.wireOp",EDGE,"E29"),sQuery(id+"F24.wireOp",EDGE,"E30.0")])],"isStart":true})});
            extrude(context, id + "F26", {"entities" : qUnion([Q0]), "operationType" : NewBodyOperationType.REMOVE, "oppositeDirection" : true, "depth" : 101.6 * mm, "offsetDistance" : 25.4 * mm});
        }
        {
            var Q0;
            Q0=makeQuery(id+"F1.opExtrude","CAP_FACE",FACE,{"disambiguationData":[OSD([sQuery(id+"F0.wireOp",EDGE,"E1")])],"isStart":false});
            var sketch = newSketch(context, id + "F27", { "sketchPlane" : qUnion([Q0])});
            skCircle(sketch, "E31", {"center": v(0, -31.75) * mm, "radius": 5.5 * mm});
            skSolve(sketch);
        }
        {
            var Q0;
            Q0 = qSketchRegion(id + "F27", true);
            extrude(context, id + "F28", {"entities" : qUnion([Q0]), "operationType" : NewBodyOperationType.REMOVE, "oppositeDirection" : true, "depth" : 152.4 * mm, "offsetDistance" : 25.4 * mm});
        }
        {
            var Q0;
            Q0=qCreatedBy(makeId("Right.planeOp"),FACE);
            var sketch = newSketch(context, id + "F29", { "sketchPlane" : qUnion([Q0])});
            skCircle(sketch, "E32.cCircle", {"center": v(0, -18.53) * mm, "radius": 2.78 * mm, "construction": true});
            skLineSegment(sketch, "E32.0", {"start": v(0, -21.74) * mm, "end": v(-2.78, -20.14) * mm});
            skLineSegment(sketch, "E32.1", {"start": v(-2.78, -20.14) * mm, "end": v(-2.78, -16.93) * mm});
            skLineSegment(sketch, "E32.2", {"start": v(-2.78, -16.93) * mm, "end": v(0, -15.32) * mm});
            skLineSegment(sketch, "E32.3", {"start": v(0, -15.32) * mm, "end": v(2.78, -16.93) * mm});
            skLineSegment(sketch, "E32.4", {"start": v(2.78, -16.93) * mm, "end": v(2.78, -20.14) * mm});
            skLineSegment(sketch, "E32.5", {"start": v(2.78, -20.14) * mm, "end": v(0, -21.74) * mm});
            skPoint(sketch, "E32.0.midPoint", {"position": v(-1.4, -20.94) * mm});
            skLineSegment(sketch, "E33.1.0.0", {"start": v(3.63, -16.91) * mm, "end": v(6.41, -15.3) * mm});
            skLineSegment(sketch, "E33.1.0.1", {"start": v(6.41, -21.73) * mm, "end": v(3.63, -20.12) * mm});
            skLineSegment(sketch, "E33.1.0.2", {"start": v(3.63, -20.12) * mm, "end": v(3.63, -16.91) * mm});
            skLineSegment(sketch, "E33.1.0.3", {"start": v(6.41, -15.3) * mm, "end": v(9.2, -16.91) * mm});
            skLineSegment(sketch, "E33.1.0.4", {"start": v(9.2, -16.91) * mm, "end": v(9.2, -20.12) * mm});
            skLineSegment(sketch, "E33.1.0.5", {"start": v(9.2, -20.12) * mm, "end": v(6.41, -21.73) * mm});
            skLineSegment(sketch, "E33.2.0.0", {"start": v(10.05, -16.9) * mm, "end": v(12.83, -15.3) * mm});
            skLineSegment(sketch, "E33.2.0.1", {"start": v(12.83, -21.72) * mm, "end": v(10.05, -20.11) * mm});
            skLineSegment(sketch, "E33.2.0.2", {"start": v(10.05, -20.11) * mm, "end": v(10.05, -16.9) * mm});
            skLineSegment(sketch, "E33.2.0.3", {"start": v(12.83, -15.3) * mm, "end": v(15.6, -16.9) * mm});
            skLineSegment(sketch, "E33.2.0.4", {"start": v(15.6, -16.9) * mm, "end": v(15.6, -20.11) * mm});
            skLineSegment(sketch, "E33.2.0.5", {"start": v(15.6, -20.11) * mm, "end": v(12.83, -21.72) * mm});
            skLineSegment(sketch, "E33.3.0.0", {"start": v(16.46, -16.9) * mm, "end": v(19.24, -15.29) * mm});
            skLineSegment(sketch, "E33.3.0.1", {"start": v(19.24, -21.7) * mm, "end": v(16.46, -20.1) * mm});
            skLineSegment(sketch, "E33.3.0.2", {"start": v(16.46, -20.1) * mm, "end": v(16.46, -16.9) * mm});
            skLineSegment(sketch, "E33.3.0.3", {"start": v(19.24, -15.29) * mm, "end": v(22.02, -16.9) * mm});
            skLineSegment(sketch, "E33.3.0.4", {"start": v(22.02, -16.9) * mm, "end": v(22.02, -20.1) * mm});
            skLineSegment(sketch, "E33.3.0.5", {"start": v(22.02, -20.1) * mm, "end": v(19.24, -21.7) * mm});
            skLineSegment(sketch, "E33.4.0.0", {"start": v(22.87, -16.88) * mm, "end": v(25.65, -15.27) * mm});
            skLineSegment(sketch, "E33.4.0.1", {"start": v(25.65, -21.7) * mm, "end": v(22.87, -20.1) * mm});
            skLineSegment(sketch, "E33.4.0.2", {"start": v(22.87, -20.1) * mm, "end": v(22.87, -16.88) * mm});
            skLineSegment(sketch, "E33.4.0.3", {"start": v(25.65, -15.27) * mm, "end": v(28.43, -16.88) * mm});
            skLineSegment(sketch, "E33.4.0.4", {"start": v(28.43, -16.88) * mm, "end": v(28.43, -20.1) * mm});
            skLineSegment(sketch, "E33.4.0.5", {"start": v(28.43, -20.1) * mm, "end": v(25.65, -21.7) * mm});
            skLineSegment(sketch, "E33.5.0.0", {"start": v(29.28, -16.87) * mm, "end": v(32.06, -15.26) * mm});
            skLineSegment(sketch, "E33.5.0.1", {"start": v(32.06, -21.69) * mm, "end": v(29.28, -20.08) * mm});
            skLineSegment(sketch, "E33.5.0.2", {"start": v(29.28, -20.08) * mm, "end": v(29.28, -16.87) * mm});
            skLineSegment(sketch, "E33.5.0.3", {"start": v(32.06, -15.26) * mm, "end": v(34.84, -16.87) * mm});
            skLineSegment(sketch, "E33.5.0.4", {"start": v(34.84, -16.87) * mm, "end": v(34.84, -20.08) * mm});
            skLineSegment(sketch, "E33.5.0.5", {"start": v(34.84, -20.08) * mm, "end": v(32.06, -21.69) * mm});
            skLineSegment(sketch, "E33.6.0.0", {"start": v(35.7, -16.86) * mm, "end": v(38.48, -15.25) * mm});
            skLineSegment(sketch, "E33.6.0.1", {"start": v(38.48, -21.67) * mm, "end": v(35.7, -20.07) * mm});
            skLineSegment(sketch, "E33.6.0.2", {"start": v(35.7, -20.07) * mm, "end": v(35.7, -16.86) * mm});
            skLineSegment(sketch, "E33.6.0.3", {"start": v(38.48, -15.25) * mm, "end": v(41.26, -16.86) * mm});
            skLineSegment(sketch, "E33.6.0.4", {"start": v(41.26, -16.86) * mm, "end": v(41.26, -20.07) * mm});
            skLineSegment(sketch, "E33.6.0.5", {"start": v(41.26, -20.07) * mm, "end": v(38.48, -21.67) * mm});
            skLineSegment(sketch, "E33.direction1", {"start": v(-2.78, -16.93) * mm, "end": v(3.63, -16.91) * mm, "construction": true});
            skLineSegment(sketch, "E34.1.0.0", {"start": v(-9.18, -16.99) * mm, "end": v(-6.4, -15.38) * mm});
            skLineSegment(sketch, "E34.1.0.1", {"start": v(-6.4, -15.38) * mm, "end": v(-3.62, -16.99) * mm});
            skLineSegment(sketch, "E34.1.0.2", {"start": v(-3.62, -16.99) * mm, "end": v(-3.62, -20.2) * mm});
            skLineSegment(sketch, "E34.1.0.3", {"start": v(-3.62, -20.2) * mm, "end": v(-6.4, -21.8) * mm});
            skLineSegment(sketch, "E34.1.0.4", {"start": v(-6.4, -21.8) * mm, "end": v(-9.18, -20.2) * mm});
            skLineSegment(sketch, "E34.1.0.5", {"start": v(-9.18, -20.2) * mm, "end": v(-9.18, -16.99) * mm});
            skLineSegment(sketch, "E34.2.0.0", {"start": v(-15.58, -17.05) * mm, "end": v(-12.8, -15.45) * mm});
            skLineSegment(sketch, "E34.2.0.1", {"start": v(-12.8, -15.45) * mm, "end": v(-10.02, -17.05) * mm});
            skLineSegment(sketch, "E34.2.0.2", {"start": v(-10.02, -17.05) * mm, "end": v(-10.02, -20.26) * mm});
            skLineSegment(sketch, "E34.2.0.3", {"start": v(-10.02, -20.26) * mm, "end": v(-12.8, -21.87) * mm});
            skLineSegment(sketch, "E34.2.0.4", {"start": v(-12.8, -21.87) * mm, "end": v(-15.58, -20.26) * mm});
            skLineSegment(sketch, "E34.2.0.5", {"start": v(-15.58, -20.26) * mm, "end": v(-15.58, -17.05) * mm});
            skLineSegment(sketch, "E34.3.0.0", {"start": v(-21.98, -17.11) * mm, "end": v(-19.2, -15.5) * mm});
            skLineSegment(sketch, "E34.3.0.1", {"start": v(-19.2, -15.5) * mm, "end": v(-16.42, -17.11) * mm});
            skLineSegment(sketch, "E34.3.0.2", {"start": v(-16.42, -17.11) * mm, "end": v(-16.42, -20.32) * mm});
            skLineSegment(sketch, "E34.3.0.3", {"start": v(-16.42, -20.32) * mm, "end": v(-19.2, -21.93) * mm});
            skLineSegment(sketch, "E34.3.0.4", {"start": v(-19.2, -21.93) * mm, "end": v(-21.98, -20.32) * mm});
            skLineSegment(sketch, "E34.3.0.5", {"start": v(-21.98, -20.32) * mm, "end": v(-21.98, -17.11) * mm});
            skLineSegment(sketch, "E34.4.0.0", {"start": v(-28.38, -17.18) * mm, "end": v(-25.6, -15.57) * mm});
            skLineSegment(sketch, "E34.4.0.1", {"start": v(-25.6, -15.57) * mm, "end": v(-22.82, -17.18) * mm});
            skLineSegment(sketch, "E34.4.0.2", {"start": v(-22.82, -17.18) * mm, "end": v(-22.82, -20.39) * mm});
            skLineSegment(sketch, "E34.4.0.3", {"start": v(-22.82, -20.39) * mm, "end": v(-25.6, -22) * mm});
            skLineSegment(sketch, "E34.4.0.4", {"start": v(-25.6, -22) * mm, "end": v(-28.38, -20.39) * mm});
            skLineSegment(sketch, "E34.4.0.5", {"start": v(-28.38, -20.39) * mm, "end": v(-28.38, -17.18) * mm});
            skLineSegment(sketch, "E34.5.0.0", {"start": v(-34.78, -17.24) * mm, "end": v(-32, -15.63) * mm});
            skLineSegment(sketch, "E34.5.0.1", {"start": v(-32, -15.63) * mm, "end": v(-29.22, -17.24) * mm});
            skLineSegment(sketch, "E34.5.0.2", {"start": v(-29.22, -17.24) * mm, "end": v(-29.22, -20.45) * mm});
            skLineSegment(sketch, "E34.5.0.3", {"start": v(-29.22, -20.45) * mm, "end": v(-32, -22.06) * mm});
            skLineSegment(sketch, "E34.5.0.4", {"start": v(-32, -22.06) * mm, "end": v(-34.78, -20.45) * mm});
            skLineSegment(sketch, "E34.5.0.5", {"start": v(-34.78, -20.45) * mm, "end": v(-34.78, -17.24) * mm});
            skLineSegment(sketch, "E34.6.0.0", {"start": v(-41.18, -17.3) * mm, "end": v(-38.4, -15.7) * mm});
            skLineSegment(sketch, "E34.6.0.1", {"start": v(-38.4, -15.7) * mm, "end": v(-35.62, -17.3) * mm});
            skLineSegment(sketch, "E34.6.0.2", {"start": v(-35.62, -17.3) * mm, "end": v(-35.62, -20.51) * mm});
            skLineSegment(sketch, "E34.6.0.3", {"start": v(-35.62, -20.51) * mm, "end": v(-38.4, -22.12) * mm});
            skLineSegment(sketch, "E34.6.0.4", {"start": v(-38.4, -22.12) * mm, "end": v(-41.18, -20.51) * mm});
            skLineSegment(sketch, "E34.6.0.5", {"start": v(-41.18, -20.51) * mm, "end": v(-41.18, -17.3) * mm});
            skLineSegment(sketch, "E34.direction1", {"start": v(-2.78, -16.93) * mm, "end": v(-9.18, -16.99) * mm, "construction": true});
            skSolve(sketch);
        }
        {
            var Q0;
            Q0=qCreatedBy(makeId("Right.planeOp"),FACE);
            var sketch = newSketch(context, id + "F30", { "sketchPlane" : qUnion([Q0])});
            skCircle(sketch, "E35.cCircle", {"center": v(-2.96, -24.58) * mm, "radius": 2.78 * mm, "construction": true});
            skLineSegment(sketch, "E35.0", {"start": v(-2.96, -27.8) * mm, "end": v(-5.74, -26.19) * mm});
            skLineSegment(sketch, "E35.1", {"start": v(-5.74, -26.19) * mm, "end": v(-5.74, -22.98) * mm});
            skLineSegment(sketch, "E35.2", {"start": v(-5.74, -22.98) * mm, "end": v(-2.96, -21.37) * mm});
            skLineSegment(sketch, "E35.3", {"start": v(-2.96, -21.37) * mm, "end": v(-0.18, -22.98) * mm});
            skLineSegment(sketch, "E35.4", {"start": v(-0.18, -22.98) * mm, "end": v(-0.18, -26.19) * mm});
            skLineSegment(sketch, "E35.5", {"start": v(-0.18, -26.19) * mm, "end": v(-2.96, -27.8) * mm});
            skPoint(sketch, "E35.0.midPoint", {"position": v(-4.35, -26.99) * mm});
            skLineSegment(sketch, "E36.1.0.0", {"start": v(0.67, -22.96) * mm, "end": v(3.45, -21.36) * mm});
            skLineSegment(sketch, "E36.1.0.1", {"start": v(3.45, -27.78) * mm, "end": v(0.67, -26.18) * mm});
            skLineSegment(sketch, "E36.1.0.2", {"start": v(0.67, -26.18) * mm, "end": v(0.67, -22.96) * mm});
            skLineSegment(sketch, "E36.1.0.3", {"start": v(3.45, -21.36) * mm, "end": v(6.23, -22.96) * mm});
            skLineSegment(sketch, "E36.1.0.4", {"start": v(6.23, -22.96) * mm, "end": v(6.23, -26.18) * mm});
            skLineSegment(sketch, "E36.1.0.5", {"start": v(6.23, -26.18) * mm, "end": v(3.45, -27.78) * mm});
            skLineSegment(sketch, "E36.2.0.0", {"start": v(7.08, -22.95) * mm, "end": v(9.86, -21.35) * mm});
            skLineSegment(sketch, "E36.2.0.1", {"start": v(9.86, -27.77) * mm, "end": v(7.08, -26.16) * mm});
            skLineSegment(sketch, "E36.2.0.2", {"start": v(7.08, -26.16) * mm, "end": v(7.08, -22.95) * mm});
            skLineSegment(sketch, "E36.2.0.3", {"start": v(9.86, -21.35) * mm, "end": v(12.64, -22.95) * mm});
            skLineSegment(sketch, "E36.2.0.4", {"start": v(12.64, -22.95) * mm, "end": v(12.64, -26.16) * mm});
            skLineSegment(sketch, "E36.2.0.5", {"start": v(12.64, -26.16) * mm, "end": v(9.86, -27.77) * mm});
            skLineSegment(sketch, "E36.3.0.0", {"start": v(13.5, -22.94) * mm, "end": v(16.27, -21.34) * mm});
            skLineSegment(sketch, "E36.3.0.1", {"start": v(16.27, -27.76) * mm, "end": v(13.5, -26.15) * mm});
            skLineSegment(sketch, "E36.3.0.2", {"start": v(13.5, -26.15) * mm, "end": v(13.5, -22.94) * mm});
            skLineSegment(sketch, "E36.3.0.3", {"start": v(16.27, -21.34) * mm, "end": v(19.05, -22.94) * mm});
            skLineSegment(sketch, "E36.3.0.4", {"start": v(19.05, -22.94) * mm, "end": v(19.05, -26.15) * mm});
            skLineSegment(sketch, "E36.3.0.5", {"start": v(19.05, -26.15) * mm, "end": v(16.27, -27.76) * mm});
            skLineSegment(sketch, "E36.4.0.0", {"start": v(19.9, -22.93) * mm, "end": v(22.69, -21.33) * mm});
            skLineSegment(sketch, "E36.4.0.1", {"start": v(22.69, -27.75) * mm, "end": v(19.9, -26.14) * mm});
            skLineSegment(sketch, "E36.4.0.2", {"start": v(19.9, -26.14) * mm, "end": v(19.9, -22.93) * mm});
            skLineSegment(sketch, "E36.4.0.3", {"start": v(22.69, -21.33) * mm, "end": v(25.47, -22.93) * mm});
            skLineSegment(sketch, "E36.4.0.4", {"start": v(25.47, -22.93) * mm, "end": v(25.47, -26.14) * mm});
            skLineSegment(sketch, "E36.4.0.5", {"start": v(25.47, -26.14) * mm, "end": v(22.69, -27.75) * mm});
            skLineSegment(sketch, "E36.5.0.0", {"start": v(26.32, -22.92) * mm, "end": v(29.1, -21.31) * mm});
            skLineSegment(sketch, "E36.5.0.1", {"start": v(29.1, -27.74) * mm, "end": v(26.32, -26.13) * mm});
            skLineSegment(sketch, "E36.5.0.2", {"start": v(26.32, -26.13) * mm, "end": v(26.32, -22.92) * mm});
            skLineSegment(sketch, "E36.5.0.3", {"start": v(29.1, -21.31) * mm, "end": v(31.88, -22.92) * mm});
            skLineSegment(sketch, "E36.5.0.4", {"start": v(31.88, -22.92) * mm, "end": v(31.88, -26.13) * mm});
            skLineSegment(sketch, "E36.5.0.5", {"start": v(31.88, -26.13) * mm, "end": v(29.1, -27.74) * mm});
            skLineSegment(sketch, "E36.6.0.0", {"start": v(32.73, -22.9) * mm, "end": v(35.51, -21.3) * mm});
            skLineSegment(sketch, "E36.6.0.1", {"start": v(35.51, -27.72) * mm, "end": v(32.73, -26.12) * mm});
            skLineSegment(sketch, "E36.6.0.2", {"start": v(32.73, -26.12) * mm, "end": v(32.73, -22.9) * mm});
            skLineSegment(sketch, "E36.6.0.3", {"start": v(35.51, -21.3) * mm, "end": v(38.3, -22.9) * mm});
            skLineSegment(sketch, "E36.6.0.4", {"start": v(38.3, -22.9) * mm, "end": v(38.3, -26.12) * mm});
            skLineSegment(sketch, "E36.6.0.5", {"start": v(38.3, -26.12) * mm, "end": v(35.51, -27.72) * mm});
            skLineSegment(sketch, "E36.direction1", {"start": v(-5.74, -22.98) * mm, "end": v(0.67, -22.96) * mm, "construction": true});
            skLineSegment(sketch, "E37.1.0.0", {"start": v(-12.15, -23.04) * mm, "end": v(-9.36, -21.43) * mm});
            skLineSegment(sketch, "E37.1.0.1", {"start": v(-9.36, -21.43) * mm, "end": v(-6.58, -23.04) * mm});
            skLineSegment(sketch, "E37.1.0.2", {"start": v(-6.58, -23.04) * mm, "end": v(-6.58, -26.25) * mm});
            skLineSegment(sketch, "E37.1.0.3", {"start": v(-6.58, -26.25) * mm, "end": v(-9.36, -27.85) * mm});
            skLineSegment(sketch, "E37.1.0.4", {"start": v(-9.36, -27.85) * mm, "end": v(-12.15, -26.25) * mm});
            skLineSegment(sketch, "E37.1.0.5", {"start": v(-12.15, -26.25) * mm, "end": v(-12.15, -23.04) * mm});
            skLineSegment(sketch, "E37.2.0.0", {"start": v(-18.55, -23.1) * mm, "end": v(-15.77, -21.5) * mm});
            skLineSegment(sketch, "E37.2.0.1", {"start": v(-15.77, -21.5) * mm, "end": v(-12.98, -23.1) * mm});
            skLineSegment(sketch, "E37.2.0.2", {"start": v(-12.98, -23.1) * mm, "end": v(-12.98, -26.31) * mm});
            skLineSegment(sketch, "E37.2.0.3", {"start": v(-12.98, -26.31) * mm, "end": v(-15.77, -27.92) * mm});
            skLineSegment(sketch, "E37.2.0.4", {"start": v(-15.77, -27.92) * mm, "end": v(-18.55, -26.31) * mm});
            skLineSegment(sketch, "E37.2.0.5", {"start": v(-18.55, -26.31) * mm, "end": v(-18.55, -23.1) * mm});
            skLineSegment(sketch, "E37.3.0.0", {"start": v(-24.95, -23.16) * mm, "end": v(-22.17, -21.56) * mm});
            skLineSegment(sketch, "E37.3.0.1", {"start": v(-22.17, -21.56) * mm, "end": v(-19.39, -23.16) * mm});
            skLineSegment(sketch, "E37.3.0.2", {"start": v(-19.39, -23.16) * mm, "end": v(-19.39, -26.37) * mm});
            skLineSegment(sketch, "E37.3.0.3", {"start": v(-19.39, -26.37) * mm, "end": v(-22.17, -27.98) * mm});
            skLineSegment(sketch, "E37.3.0.4", {"start": v(-22.17, -27.98) * mm, "end": v(-24.95, -26.37) * mm});
            skLineSegment(sketch, "E37.3.0.5", {"start": v(-24.95, -26.37) * mm, "end": v(-24.95, -23.16) * mm});
            skLineSegment(sketch, "E37.4.0.0", {"start": v(-31.35, -23.23) * mm, "end": v(-28.57, -21.62) * mm});
            skLineSegment(sketch, "E37.4.0.1", {"start": v(-28.57, -21.62) * mm, "end": v(-25.79, -23.23) * mm});
            skLineSegment(sketch, "E37.4.0.2", {"start": v(-25.79, -23.23) * mm, "end": v(-25.79, -26.44) * mm});
            skLineSegment(sketch, "E37.4.0.3", {"start": v(-25.79, -26.44) * mm, "end": v(-28.57, -28.04) * mm});
            skLineSegment(sketch, "E37.4.0.4", {"start": v(-28.57, -28.04) * mm, "end": v(-31.35, -26.44) * mm});
            skLineSegment(sketch, "E37.4.0.5", {"start": v(-31.35, -26.44) * mm, "end": v(-31.35, -23.23) * mm});
            skLineSegment(sketch, "E37.5.0.0", {"start": v(-37.75, -23.29) * mm, "end": v(-34.97, -21.68) * mm});
            skLineSegment(sketch, "E37.5.0.1", {"start": v(-34.97, -21.68) * mm, "end": v(-32.19, -23.29) * mm});
            skLineSegment(sketch, "E37.5.0.2", {"start": v(-32.19, -23.29) * mm, "end": v(-32.19, -26.5) * mm});
            skLineSegment(sketch, "E37.5.0.3", {"start": v(-32.19, -26.5) * mm, "end": v(-34.97, -28.1) * mm});
            skLineSegment(sketch, "E37.5.0.4", {"start": v(-34.97, -28.1) * mm, "end": v(-37.75, -26.5) * mm});
            skLineSegment(sketch, "E37.5.0.5", {"start": v(-37.75, -26.5) * mm, "end": v(-37.75, -23.29) * mm});
            skLineSegment(sketch, "E37.6.0.0", {"start": v(-44.15, -23.35) * mm, "end": v(-41.37, -21.75) * mm});
            skLineSegment(sketch, "E37.6.0.1", {"start": v(-41.37, -21.75) * mm, "end": v(-38.59, -23.35) * mm});
            skLineSegment(sketch, "E37.6.0.2", {"start": v(-38.59, -23.35) * mm, "end": v(-38.59, -26.56) * mm});
            skLineSegment(sketch, "E37.6.0.3", {"start": v(-38.59, -26.56) * mm, "end": v(-41.37, -28.17) * mm});
            skLineSegment(sketch, "E37.6.0.4", {"start": v(-41.37, -28.17) * mm, "end": v(-44.15, -26.56) * mm});
            skLineSegment(sketch, "E37.6.0.5", {"start": v(-44.15, -26.56) * mm, "end": v(-44.15, -23.35) * mm});
            skLineSegment(sketch, "E37.direction1", {"start": v(-5.74, -22.98) * mm, "end": v(-12.15, -23.04) * mm, "construction": true});
            skLineSegment(sketch, "E38.0.7.0", {"start": v(39.14, -22.9) * mm, "end": v(41.93, -21.3) * mm});
            skLineSegment(sketch, "E38.3.7.0", {"start": v(41.93, -27.71) * mm, "end": v(39.14, -26.1) * mm});
            skLineSegment(sketch, "E38.6.7.0", {"start": v(39.14, -26.1) * mm, "end": v(39.14, -22.9) * mm});
            skLineSegment(sketch, "E38.9.7.0", {"start": v(41.93, -21.3) * mm, "end": v(44.7, -22.9) * mm});
            skLineSegment(sketch, "E38.12.7.0", {"start": v(44.7, -22.9) * mm, "end": v(44.7, -26.1) * mm});
            skLineSegment(sketch, "E38.15.7.0", {"start": v(44.7, -26.1) * mm, "end": v(41.93, -27.71) * mm});
            skCircle(sketch, "E39.cCircle", {"center": v(-3.31, -12.84) * mm, "radius": 2.78 * mm, "construction": true});
            skLineSegment(sketch, "E39.0", {"start": v(-3.31, -16.05) * mm, "end": v(-6.1, -14.44) * mm});
            skLineSegment(sketch, "E39.1", {"start": v(-6.1, -14.44) * mm, "end": v(-6.1, -11.23) * mm});
            skLineSegment(sketch, "E39.2", {"start": v(-6.1, -11.23) * mm, "end": v(-3.31, -9.62) * mm});
            skLineSegment(sketch, "E39.3", {"start": v(-3.31, -9.62) * mm, "end": v(-0.53, -11.23) * mm});
            skLineSegment(sketch, "E39.4", {"start": v(-0.53, -11.23) * mm, "end": v(-0.53, -14.44) * mm});
            skLineSegment(sketch, "E39.5", {"start": v(-0.53, -14.44) * mm, "end": v(-3.31, -16.05) * mm});
            skPoint(sketch, "E39.0.midPoint", {"position": v(-4.7, -15.24) * mm});
            skLineSegment(sketch, "E40.1.0.0", {"start": v(0.32, -11.22) * mm, "end": v(3.1, -9.61) * mm});
            skLineSegment(sketch, "E40.1.0.1", {"start": v(3.1, -16.04) * mm, "end": v(0.32, -14.43) * mm});
            skLineSegment(sketch, "E40.1.0.2", {"start": v(0.32, -14.43) * mm, "end": v(0.32, -11.22) * mm});
            skLineSegment(sketch, "E40.1.0.3", {"start": v(3.1, -9.61) * mm, "end": v(5.88, -11.22) * mm});
            skLineSegment(sketch, "E40.1.0.4", {"start": v(5.88, -11.22) * mm, "end": v(5.88, -14.43) * mm});
            skLineSegment(sketch, "E40.1.0.5", {"start": v(5.88, -14.43) * mm, "end": v(3.1, -16.04) * mm});
            skLineSegment(sketch, "E40.2.0.0", {"start": v(6.73, -11.2) * mm, "end": v(9.51, -9.6) * mm});
            skLineSegment(sketch, "E40.2.0.1", {"start": v(9.51, -16.02) * mm, "end": v(6.73, -14.42) * mm});
            skLineSegment(sketch, "E40.2.0.2", {"start": v(6.73, -14.42) * mm, "end": v(6.73, -11.2) * mm});
            skLineSegment(sketch, "E40.2.0.3", {"start": v(9.51, -9.6) * mm, "end": v(12.3, -11.2) * mm});
            skLineSegment(sketch, "E40.2.0.4", {"start": v(12.3, -11.2) * mm, "end": v(12.3, -14.42) * mm});
            skLineSegment(sketch, "E40.2.0.5", {"start": v(12.3, -14.42) * mm, "end": v(9.51, -16.02) * mm});
            skLineSegment(sketch, "E40.3.0.0", {"start": v(13.14, -11.2) * mm, "end": v(15.93, -9.6) * mm});
            skLineSegment(sketch, "E40.3.0.1", {"start": v(15.93, -16.01) * mm, "end": v(13.14, -14.4) * mm});
            skLineSegment(sketch, "E40.3.0.2", {"start": v(13.14, -14.4) * mm, "end": v(13.14, -11.2) * mm});
            skLineSegment(sketch, "E40.3.0.3", {"start": v(15.93, -9.6) * mm, "end": v(18.7, -11.2) * mm});
            skLineSegment(sketch, "E40.3.0.4", {"start": v(18.7, -11.2) * mm, "end": v(18.7, -14.4) * mm});
            skLineSegment(sketch, "E40.3.0.5", {"start": v(18.7, -14.4) * mm, "end": v(15.93, -16.01) * mm});
            skLineSegment(sketch, "E40.4.0.0", {"start": v(19.56, -11.19) * mm, "end": v(22.34, -9.58) * mm});
            skLineSegment(sketch, "E40.4.0.1", {"start": v(22.34, -16) * mm, "end": v(19.56, -14.4) * mm});
            skLineSegment(sketch, "E40.4.0.2", {"start": v(19.56, -14.4) * mm, "end": v(19.56, -11.19) * mm});
            skLineSegment(sketch, "E40.4.0.3", {"start": v(22.34, -9.58) * mm, "end": v(25.12, -11.19) * mm});
            skLineSegment(sketch, "E40.4.0.4", {"start": v(25.12, -11.19) * mm, "end": v(25.12, -14.4) * mm});
            skLineSegment(sketch, "E40.4.0.5", {"start": v(25.12, -14.4) * mm, "end": v(22.34, -16) * mm});
            skLineSegment(sketch, "E40.5.0.0", {"start": v(25.97, -11.17) * mm, "end": v(28.75, -9.57) * mm});
            skLineSegment(sketch, "E40.5.0.1", {"start": v(28.75, -15.99) * mm, "end": v(25.97, -14.38) * mm});
            skLineSegment(sketch, "E40.5.0.2", {"start": v(25.97, -14.38) * mm, "end": v(25.97, -11.17) * mm});
            skLineSegment(sketch, "E40.5.0.3", {"start": v(28.75, -9.57) * mm, "end": v(31.53, -11.17) * mm});
            skLineSegment(sketch, "E40.5.0.4", {"start": v(31.53, -11.17) * mm, "end": v(31.53, -14.38) * mm});
            skLineSegment(sketch, "E40.5.0.5", {"start": v(31.53, -14.38) * mm, "end": v(28.75, -15.99) * mm});
            skLineSegment(sketch, "E40.6.0.0", {"start": v(32.38, -11.16) * mm, "end": v(35.16, -9.56) * mm});
            skLineSegment(sketch, "E40.6.0.1", {"start": v(35.16, -15.98) * mm, "end": v(32.38, -14.37) * mm});
            skLineSegment(sketch, "E40.6.0.2", {"start": v(32.38, -14.37) * mm, "end": v(32.38, -11.16) * mm});
            skLineSegment(sketch, "E40.6.0.3", {"start": v(35.16, -9.56) * mm, "end": v(37.94, -11.16) * mm});
            skLineSegment(sketch, "E40.6.0.4", {"start": v(37.94, -11.16) * mm, "end": v(37.94, -14.37) * mm});
            skLineSegment(sketch, "E40.6.0.5", {"start": v(37.94, -14.37) * mm, "end": v(35.16, -15.98) * mm});
            skLineSegment(sketch, "E40.direction1", {"start": v(-6.1, -11.23) * mm, "end": v(0.32, -11.22) * mm, "construction": true});
            skLineSegment(sketch, "E41.1.0.0", {"start": v(-12.5, -11.3) * mm, "end": v(-9.71, -9.69) * mm});
            skLineSegment(sketch, "E41.1.0.1", {"start": v(-9.71, -9.69) * mm, "end": v(-6.93, -11.3) * mm});
            skLineSegment(sketch, "E41.1.0.2", {"start": v(-6.93, -11.3) * mm, "end": v(-6.93, -14.5) * mm});
            skLineSegment(sketch, "E41.1.0.3", {"start": v(-6.93, -14.5) * mm, "end": v(-9.71, -16.1) * mm});
            skLineSegment(sketch, "E41.1.0.4", {"start": v(-9.71, -16.1) * mm, "end": v(-12.5, -14.5) * mm});
            skLineSegment(sketch, "E41.1.0.5", {"start": v(-12.5, -14.5) * mm, "end": v(-12.5, -11.3) * mm});
            skLineSegment(sketch, "E41.2.0.0", {"start": v(-18.9, -11.36) * mm, "end": v(-16.11, -9.75) * mm});
            skLineSegment(sketch, "E41.2.0.1", {"start": v(-16.11, -9.75) * mm, "end": v(-13.33, -11.36) * mm});
            skLineSegment(sketch, "E41.2.0.2", {"start": v(-13.33, -11.36) * mm, "end": v(-13.33, -14.57) * mm});
            skLineSegment(sketch, "E41.2.0.3", {"start": v(-13.33, -14.57) * mm, "end": v(-16.11, -16.17) * mm});
            skLineSegment(sketch, "E41.2.0.4", {"start": v(-16.11, -16.17) * mm, "end": v(-18.9, -14.57) * mm});
            skLineSegment(sketch, "E41.2.0.5", {"start": v(-18.9, -14.57) * mm, "end": v(-18.9, -11.36) * mm});
            skLineSegment(sketch, "E41.3.0.0", {"start": v(-25.3, -11.42) * mm, "end": v(-22.51, -9.81) * mm});
            skLineSegment(sketch, "E41.3.0.1", {"start": v(-22.51, -9.81) * mm, "end": v(-19.73, -11.42) * mm});
            skLineSegment(sketch, "E41.3.0.2", {"start": v(-19.73, -11.42) * mm, "end": v(-19.73, -14.63) * mm});
            skLineSegment(sketch, "E41.3.0.3", {"start": v(-19.73, -14.63) * mm, "end": v(-22.51, -16.23) * mm});
            skLineSegment(sketch, "E41.3.0.4", {"start": v(-22.51, -16.23) * mm, "end": v(-25.3, -14.63) * mm});
            skLineSegment(sketch, "E41.3.0.5", {"start": v(-25.3, -14.63) * mm, "end": v(-25.3, -11.42) * mm});
            skLineSegment(sketch, "E41.4.0.0", {"start": v(-31.7, -11.48) * mm, "end": v(-28.92, -9.88) * mm});
            skLineSegment(sketch, "E41.4.0.1", {"start": v(-28.92, -9.88) * mm, "end": v(-26.13, -11.48) * mm});
            skLineSegment(sketch, "E41.4.0.2", {"start": v(-26.13, -11.48) * mm, "end": v(-26.13, -14.7) * mm});
            skLineSegment(sketch, "E41.4.0.3", {"start": v(-26.13, -14.7) * mm, "end": v(-28.92, -16.3) * mm});
            skLineSegment(sketch, "E41.4.0.4", {"start": v(-28.92, -16.3) * mm, "end": v(-31.7, -14.7) * mm});
            skLineSegment(sketch, "E41.4.0.5", {"start": v(-31.7, -14.7) * mm, "end": v(-31.7, -11.48) * mm});
            skLineSegment(sketch, "E41.5.0.0", {"start": v(-38.1, -11.54) * mm, "end": v(-35.32, -9.94) * mm});
            skLineSegment(sketch, "E41.5.0.1", {"start": v(-35.32, -9.94) * mm, "end": v(-32.53, -11.54) * mm});
            skLineSegment(sketch, "E41.5.0.2", {"start": v(-32.53, -11.54) * mm, "end": v(-32.53, -14.75) * mm});
            skLineSegment(sketch, "E41.5.0.3", {"start": v(-32.53, -14.75) * mm, "end": v(-35.32, -16.36) * mm});
            skLineSegment(sketch, "E41.5.0.4", {"start": v(-35.32, -16.36) * mm, "end": v(-38.1, -14.75) * mm});
            skLineSegment(sketch, "E41.5.0.5", {"start": v(-38.1, -14.75) * mm, "end": v(-38.1, -11.54) * mm});
            skLineSegment(sketch, "E41.6.0.0", {"start": v(-44.5, -11.6) * mm, "end": v(-41.72, -10) * mm});
            skLineSegment(sketch, "E41.6.0.1", {"start": v(-41.72, -10) * mm, "end": v(-38.94, -11.6) * mm});
            skLineSegment(sketch, "E41.6.0.2", {"start": v(-38.94, -11.6) * mm, "end": v(-38.94, -14.82) * mm});
            skLineSegment(sketch, "E41.6.0.3", {"start": v(-38.94, -14.82) * mm, "end": v(-41.72, -16.42) * mm});
            skLineSegment(sketch, "E41.6.0.4", {"start": v(-41.72, -16.42) * mm, "end": v(-44.5, -14.82) * mm});
            skLineSegment(sketch, "E41.6.0.5", {"start": v(-44.5, -14.82) * mm, "end": v(-44.5, -11.6) * mm});
            skLineSegment(sketch, "E41.direction1", {"start": v(-6.1, -11.23) * mm, "end": v(-12.5, -11.3) * mm, "construction": true});
            skLineSegment(sketch, "E42.0.7.0", {"start": v(38.8, -11.15) * mm, "end": v(41.58, -9.55) * mm});
            skLineSegment(sketch, "E42.3.7.0", {"start": v(41.58, -15.97) * mm, "end": v(38.8, -14.36) * mm});
            skLineSegment(sketch, "E42.6.7.0", {"start": v(38.8, -14.36) * mm, "end": v(38.8, -11.15) * mm});
            skLineSegment(sketch, "E42.9.7.0", {"start": v(41.58, -9.55) * mm, "end": v(44.36, -11.15) * mm});
            skLineSegment(sketch, "E42.12.7.0", {"start": v(44.36, -11.15) * mm, "end": v(44.36, -14.36) * mm});
            skLineSegment(sketch, "E42.15.7.0", {"start": v(44.36, -14.36) * mm, "end": v(41.58, -15.97) * mm});
            skSolve(sketch);
        }
        {
            var Q0;
            Q0 = qSketchRegion(id + "F30", true);
            var Q1;
            Q1 = qSketchRegion(id + "F29", true);
            extrude(context, id + "F31", {"entities" : qUnion([Q0, Q1]), "operationType" : NewBodyOperationType.REMOVE, "endBound" : BoundingType.SYMMETRIC, "oppositeDirection" : true, "depth" : 127 * mm, "offsetDistance" : 25.4 * mm});
        }
        {
            var Q0;
            {var subQ0=makeQuery(id+"F10.opExtrude","CAP_FACE",FACE,{"disambiguationData":[OSD([sQuery(id+"F9.wireOp",EDGE,"E9")])],"isStart":false});var subQ1=makeQuery(id+"F8.opExtrude","CAP_FACE",FACE,{"disambiguationData":[OSD([sQuery(id+"F7.wireOp",EDGE,"E4.0"),sQuery(id+"F7.wireOp",EDGE,"E5.0"),sQuery(id+"F7.wireOp",EDGE,"E7"),sQuery(id+"F7.wireOp",EDGE,"E8")])],"isStart":true});var subQ2=sQuery(id+"F24.wireOp",EDGE,"E29");var subQ3=makeQuery(id+"F25.opExtrude","SWEPT_FACE",FACE,{"disambiguationData":[OSD([subQ2])]});var subQ4=makeQuery(id+"F25.opExtrude","CAP_FACE",FACE,{"disambiguationData":[OSD([subQ2,sQuery(id+"F24.wireOp",EDGE,"E30.0")])],"isStart":true});Q0=makeQuery(id+"F25.boolean.opBoolean","SPLIT",EDGE,{"disambiguationData":[topologyDisambiguationEdgeConnected([subQ1,subQ0,subQ3,subQ4]),TD([makeQuery(id+"F18.boolean.opBoolean","COPY",FACE,{"derivedFrom":makeQuery(id+"F18.opExtrude","SWEPT_FACE",FACE,{"disambiguationData":[OSD([sQuery(id+"F17.wireOp",EDGE,"E16.4")])]})})])],"derivedFrom":makeQuery(id+"F25.opExtrude","CAP_EDGE",EDGE,{"disambiguationData":[OSD([subQ2])],"isStart":true})});}
            var Q1;
            {var subQ0=sQuery(id+"F9.wireOp",EDGE,"E9");var subQ1=makeQuery(id+"F10.opExtrude","SWEPT_FACE",FACE,{"disambiguationData":[OSD([subQ0])]});var subQ2=makeQuery(id+"F10.opExtrude","CAP_FACE",FACE,{"disambiguationData":[OSD([subQ0])],"isStart":false});var subQ3=makeQuery(id+"F8.opExtrude","CAP_FACE",FACE,{"disambiguationData":[OSD([sQuery(id+"F7.wireOp",EDGE,"E4.0"),sQuery(id+"F7.wireOp",EDGE,"E5.0"),sQuery(id+"F7.wireOp",EDGE,"E7"),sQuery(id+"F7.wireOp",EDGE,"E8")])],"isStart":true});Q1=makeQuery(id+"F18.boolean.opBoolean","SPLIT",EDGE,{"disambiguationData":[TD([makeQuery(id+"F1.opExtrude","SWEPT_FACE",FACE,{"disambiguationData":[OSD([sQuery(id+"F0.wireOp",EDGE,"E0")])]})])],"derivedFrom":makeQuery(id+"F10.boolean.opBoolean","SPLIT",EDGE,{"disambiguationData":[topologyDisambiguationEdgeConnected([subQ3,subQ1,subQ2]),OD(1.0)],"derivedFrom":makeQuery(id+"F10.opExtrude","CAP_EDGE",EDGE,{"disambiguationData":[OSD([subQ0])],"isStart":false})})});}
            var Q2;
            {var subQ0=sQuery(id+"F9.wireOp",EDGE,"E9");var subQ1=sQuery(id+"F24.wireOp",EDGE,"E29");var subQ2=makeQuery(id+"F25.opExtrude","CAP_FACE",FACE,{"disambiguationData":[OSD([subQ1,sQuery(id+"F24.wireOp",EDGE,"E30.0")])],"isStart":true});var subQ3=makeQuery(id+"F10.opExtrude","CAP_FACE",FACE,{"disambiguationData":[OSD([subQ0])],"isStart":false});var subQ4=makeQuery(id+"F8.opExtrude","CAP_FACE",FACE,{"disambiguationData":[OSD([sQuery(id+"F7.wireOp",EDGE,"E4.0"),sQuery(id+"F7.wireOp",EDGE,"E5.0"),sQuery(id+"F7.wireOp",EDGE,"E7"),sQuery(id+"F7.wireOp",EDGE,"E8")])],"isStart":true});var subQ5=makeQuery(id+"F25.opExtrude","SWEPT_FACE",FACE,{"disambiguationData":[OSD([subQ1])]});Q2=makeQuery(id+"F25.boolean.opBoolean","SPLIT",EDGE,{"disambiguationData":[topologyDisambiguationEdgeConnected([subQ4,subQ3,subQ5,subQ2]),TD([makeQuery(id+"F10.opExtrude","SWEPT_FACE",FACE,{"disambiguationData":[OSD([subQ0])]})])],"derivedFrom":makeQuery(id+"F25.opExtrude","CAP_EDGE",EDGE,{"disambiguationData":[OSD([subQ1])],"isStart":true})});}
            fillet(context, id + "F32", {"entities" : qUnion([Q0, Q1, Q2]), "radius" : 5.08 * mm, "tangentPropagation" : true, "allowEdgeOverflow" : false});
        }
        {
            var Q0;
            {var subQ0=sQuery(id+"F9.wireOp",EDGE,"E9");var subQ1=makeQuery(id+"F10.opExtrude","SWEPT_FACE",FACE,{"disambiguationData":[OSD([subQ0])]});var subQ2=makeQuery(id+"F10.opExtrude","CAP_FACE",FACE,{"disambiguationData":[OSD([subQ0])],"isStart":false});var subQ3=makeQuery(id+"F8.opExtrude","CAP_FACE",FACE,{"disambiguationData":[OSD([sQuery(id+"F7.wireOp",EDGE,"E4.0"),sQuery(id+"F7.wireOp",EDGE,"E5.0"),sQuery(id+"F7.wireOp",EDGE,"E7"),sQuery(id+"F7.wireOp",EDGE,"E8")])],"isStart":true});Q0=makeQuery(id+"F18.boolean.opBoolean","SPLIT",EDGE,{"disambiguationData":[TD([makeQuery(id+"F1.opExtrude","SWEPT_FACE",FACE,{"disambiguationData":[OSD([sQuery(id+"F0.wireOp",EDGE,"E0")])]})])],"derivedFrom":makeQuery(id+"F10.boolean.opBoolean","SPLIT",EDGE,{"disambiguationData":[topologyDisambiguationEdgeConnected([subQ3,subQ1,subQ2]),OD(0.0)],"derivedFrom":makeQuery(id+"F10.opExtrude","CAP_EDGE",EDGE,{"disambiguationData":[OSD([subQ0])],"isStart":false})})});}
            fillet(context, id + "F33", {"entities" : qUnion([Q0]), "radius" : 5.08 * mm, "tangentPropagation" : true, "allowEdgeOverflow" : false});
        }
        {
            var Q0;
            {var subQ0=sQuery(id+"F9.wireOp",EDGE,"E9");var subQ1=makeQuery(id+"F10.opExtrude","CAP_FACE",FACE,{"disambiguationData":[OSD([subQ0])],"isStart":true});var subQ2=sQuery(id+"F24.wireOp",EDGE,"E29");var subQ3=makeQuery(id+"F25.opExtrude","CAP_FACE",FACE,{"disambiguationData":[OSD([subQ2,sQuery(id+"F24.wireOp",EDGE,"E30.0")])],"isStart":false});var subQ4=makeQuery(id+"F8.opExtrude","CAP_FACE",FACE,{"disambiguationData":[OSD([sQuery(id+"F7.wireOp",EDGE,"E4.0"),sQuery(id+"F7.wireOp",EDGE,"E5.0"),sQuery(id+"F7.wireOp",EDGE,"E7"),sQuery(id+"F7.wireOp",EDGE,"E8")])],"isStart":false});var subQ5=makeQuery(id+"F25.opExtrude","SWEPT_FACE",FACE,{"disambiguationData":[OSD([subQ2])]});Q0=makeQuery(id+"F25.boolean.opBoolean","SPLIT",EDGE,{"disambiguationData":[topologyDisambiguationEdgeConnected([subQ4,subQ1,subQ5,subQ3]),TD([makeQuery(id+"F10.opExtrude","SWEPT_FACE",FACE,{"disambiguationData":[OSD([subQ0])]})])],"derivedFrom":makeQuery(id+"F25.opExtrude","CAP_EDGE",EDGE,{"disambiguationData":[OSD([subQ2])],"isStart":false})});}
            var Q1;
            {var subQ0=makeQuery(id+"F10.opExtrude","CAP_FACE",FACE,{"disambiguationData":[OSD([sQuery(id+"F9.wireOp",EDGE,"E9")])],"isStart":true});var subQ1=sQuery(id+"F24.wireOp",EDGE,"E29");var subQ2=makeQuery(id+"F25.opExtrude","CAP_FACE",FACE,{"disambiguationData":[OSD([subQ1,sQuery(id+"F24.wireOp",EDGE,"E30.0")])],"isStart":false});var subQ3=makeQuery(id+"F8.opExtrude","CAP_FACE",FACE,{"disambiguationData":[OSD([sQuery(id+"F7.wireOp",EDGE,"E4.0"),sQuery(id+"F7.wireOp",EDGE,"E5.0"),sQuery(id+"F7.wireOp",EDGE,"E7"),sQuery(id+"F7.wireOp",EDGE,"E8")])],"isStart":false});var subQ4=makeQuery(id+"F25.opExtrude","SWEPT_FACE",FACE,{"disambiguationData":[OSD([subQ1])]});Q1=makeQuery(id+"F25.boolean.opBoolean","SPLIT",EDGE,{"disambiguationData":[topologyDisambiguationEdgeConnected([subQ3,subQ0,subQ4,subQ2]),TD([makeQuery(id+"F18.boolean.opBoolean","COPY",FACE,{"derivedFrom":makeQuery(id+"F18.opExtrude","SWEPT_FACE",FACE,{"disambiguationData":[OSD([sQuery(id+"F17.wireOp",EDGE,"E16.4")])]})})])],"derivedFrom":makeQuery(id+"F25.opExtrude","CAP_EDGE",EDGE,{"disambiguationData":[OSD([subQ1])],"isStart":false})});}
            fillet(context, id + "F34", {"entities" : qUnion([Q0, Q1]), "radius" : 5.08 * mm, "tangentPropagation" : true, "allowEdgeOverflow" : false});
        }
        {
            var Q0;
            {var subQ0=sQuery(id+"F9.wireOp",EDGE,"E9");var subQ1=makeQuery(id+"F10.opExtrude","CAP_FACE",FACE,{"disambiguationData":[OSD([subQ0])],"isStart":true});var subQ2=makeQuery(id+"F10.opExtrude","SWEPT_FACE",FACE,{"disambiguationData":[OSD([subQ0])]});var subQ3=makeQuery(id+"F8.opExtrude","CAP_FACE",FACE,{"disambiguationData":[OSD([sQuery(id+"F7.wireOp",EDGE,"E4.0"),sQuery(id+"F7.wireOp",EDGE,"E5.0"),sQuery(id+"F7.wireOp",EDGE,"E7"),sQuery(id+"F7.wireOp",EDGE,"E8")])],"isStart":false});Q0=makeQuery(id+"F18.boolean.opBoolean","SPLIT",EDGE,{"disambiguationData":[TD([makeQuery(id+"F1.opExtrude","SWEPT_FACE",FACE,{"disambiguationData":[OSD([sQuery(id+"F0.wireOp",EDGE,"E0")])]})])],"derivedFrom":makeQuery(id+"F10.boolean.opBoolean","SPLIT",EDGE,{"disambiguationData":[topologyDisambiguationEdgeConnected([subQ3,subQ2,subQ1]),OD(0.0)],"derivedFrom":makeQuery(id+"F10.opExtrude","CAP_EDGE",EDGE,{"disambiguationData":[OSD([subQ0])],"isStart":true})})});}
            fillet(context, id + "F35", {"entities" : qUnion([Q0]), "radius" : 5.08 * mm, "tangentPropagation" : true, "allowEdgeOverflow" : false});
        }
    });
